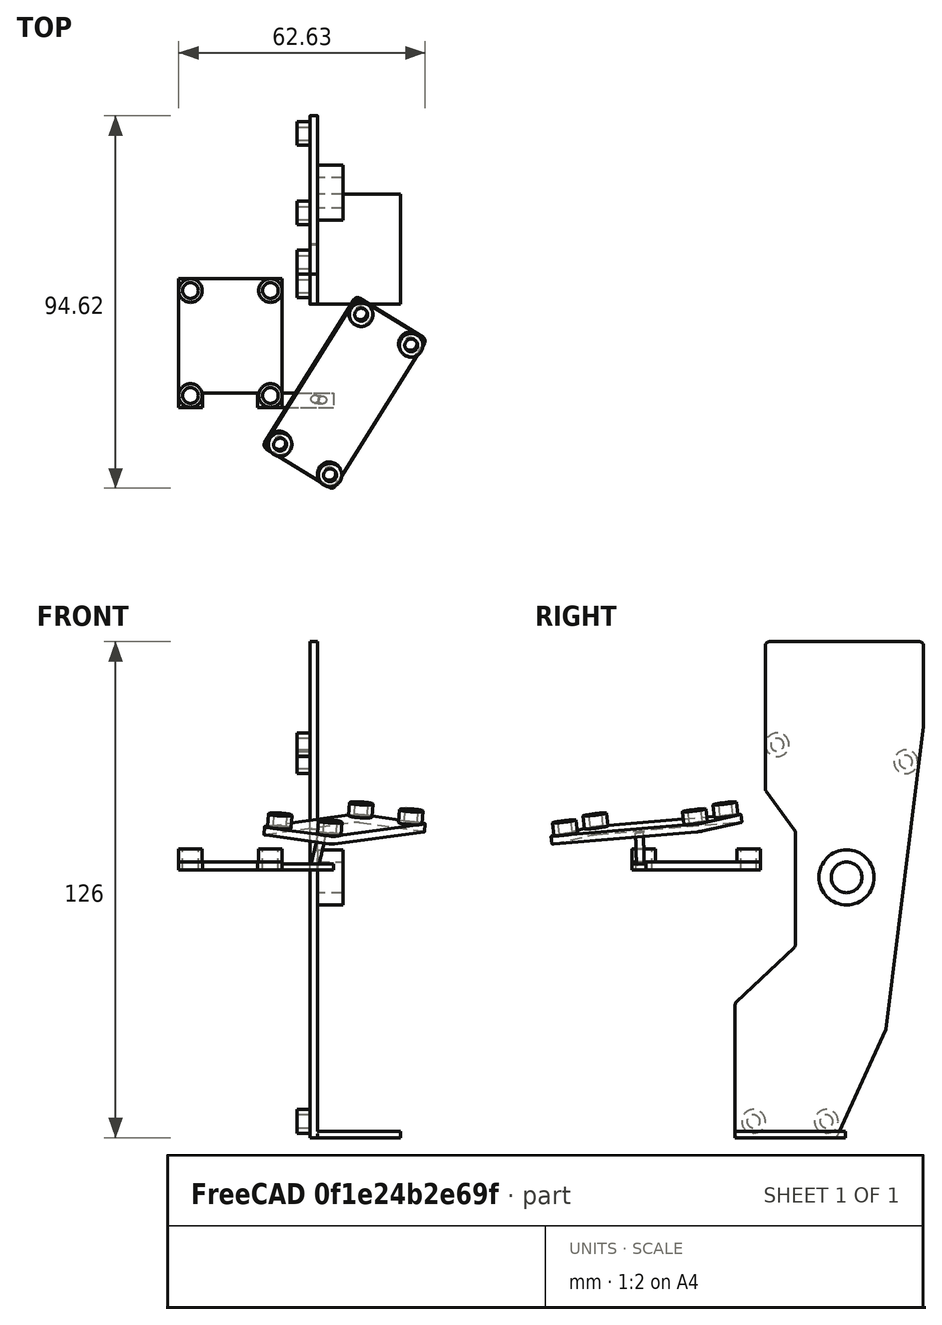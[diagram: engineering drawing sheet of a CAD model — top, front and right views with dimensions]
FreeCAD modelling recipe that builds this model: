
FCSTD DOCUMENT  (FreeCAD 1.0RUnknown)
Label: case-vertical
License: All rights reserved
LicenseURL: https://en.wikipedia.org/wiki/All_rights_reserved
objects: Sketcher::SketchObject×13, PartDesign::Pad×10, App::Link×10, App::FeaturePython×10, PartDesign::Body×3, PartDesign::Pocket×2, Assembly::JointGroup×1, Assembly::AssemblyObject×1, App::Part×1
note: 65 computed .brp shape members not serialized (recipe doc carries the construction recipe); baked Part::Feature solids carry a one-line shape summary decoded from their .brp
EXTERNAL_REF file=left.FCStd obj=Board_f9e4
EXTERNAL_REF file=thumbstick-breakout.FCStd obj=Board_bbd4
EXTERNAL_REF file=thumbstick.FCStd obj=Joystick_v6
EXTERNAL_REF file=thumb-cluster.FCStd obj=Board_58ce
EXTERNAL_REF file=caps.FCStd obj=Body001
EXTERNAL_REF file=caps.FCStd obj=Body
EXTERNAL_REF file=trackball-holder.FCStd obj=Part

FEATURE [Sketcher::SketchObject] PCB_Sketch_f9e4  label="left"
  ArcFitTolerance = 1e-06
  FullyConstrained = false
  MakeInternals = false
  MapMode = 5
  Placement = pos=(0,0,0) rot=(0,-1,0;1.5708rad)
  sketch-geometry (21):
    g0: LineSegment StartX=48.9342 StartY=15.25 StartZ=0 EndX=77.5946 EndY=15.25 EndZ=0
    g1: LineSegment StartX=27.2503 StartY=38.2054 StartZ=0 EndX=0.583058 EndY=26.0175 EndZ=0
    g2: LineSegment StartX=126 StartY=8.65 StartZ=0 EndX=126 EndY=45.95 EndZ=0
    g3: LineSegment StartX=9e-16 StartY=25.1085 StartZ=0 EndX=0 EndY=1 EndZ=0
    g4: LineSegment StartX=104.439 StartY=47.8424 StartZ=0 EndX=27.5489 EndY=38.289 EndZ=0
    g5: LineSegment StartX=34.5465 StartY=0.317255 StartZ=0 EndX=48.2035 EndY=14.9327 EndZ=0
    g6: LineSegment StartX=104.562 StartY=47.85 StartZ=0 EndX=125 EndY=47.85 EndZ=0
    g7: LineSegment StartX=125 StartY=7.65 StartZ=0 EndX=88.6266 EndY=7.65 EndZ=0
    g8: LineSegment StartX=1 StartY=1e-16 StartZ=0 EndX=33.8158 EndY=-1.6e-15 EndZ=0
    g9: LineSegment StartX=126 StartY=45.95 StartZ=0 EndX=126 EndY=46.85 EndZ=0
    g10: LineSegment StartX=78.291 StartY=14.9676 StartZ=0 EndX=88.0364 EndY=7.84274 EndZ=0
    g11: ArcOfCircle CenterX=27.666 CenterY=37.2959 CenterZ=0 NormalX=0 NormalY=0 NormalZ=-1 AngleXU=1.14211 Radius=1.00001 StartAngle=0 EndAngle=0.311303
    g12: ArcOfCircle CenterX=33.8158 CenterY=1.00002 CenterZ=0 NormalX=0 NormalY=0 NormalZ=-1 AngleXU=-2.39007 Radius=1.00002 StartAngle=0 EndAngle=0.81927
    g13: ArcOfCircle CenterX=48.9342 CenterY=14.25 CenterZ=0 NormalX=0 NormalY=0 NormalZ=-1 AngleXU=0.75152 Radius=1.00002 StartAngle=0 EndAngle=0.81927
    g14: ArcOfCircle CenterX=125 CenterY=46.85 CenterZ=0 NormalX=0 NormalY=0 NormalZ=-1 AngleXU=1.5708 Radius=0.999999 StartAngle=0 EndAngle=1.5708
    g15: ArcOfCircle CenterX=125 CenterY=8.65 CenterZ=0 NormalX=0 NormalY=0 NormalZ=-1 AngleXU=3.14159 Radius=0.999999 StartAngle=0 EndAngle=1.5708
    g16: ArcOfCircle CenterX=88.6266 CenterY=8.65 CenterZ=0 NormalX=0 NormalY=0 NormalZ=-1 AngleXU=-1.57079 Radius=1 StartAngle=0 EndAngle=0.631296
    g17: ArcOfCircle CenterX=104.562 CenterY=46.8498 CenterZ=0 NormalX=0 NormalY=0 NormalZ=-1 AngleXU=1.44719 Radius=1.00016 StartAngle=0 EndAngle=0.123594
    g18: ArcOfCircle CenterX=0.999999 CenterY=0.999999 CenterZ=0 NormalX=0 NormalY=0 NormalZ=-1 AngleXU=-1.5708 Radius=0.999999 StartAngle=0 EndAngle=1.5708
    g19: ArcOfCircle CenterX=1.00007 CenterY=25.1085 CenterZ=0 NormalX=0 NormalY=0 NormalZ=-1 AngleXU=4.52044e-05 Radius=1.00007 StartAngle=0 EndAngle=1.14063
    g20: ArcOfCircle CenterX=77.5946 CenterY=14.25 CenterZ=0 NormalX=0 NormalY=0 NormalZ=-1 AngleXU=1.57078 Radius=0.999961 StartAngle=0 EndAngle=0.770416
  constraints (21):
    c: Coincident(g3,g18)
    c: Coincident(g3,g19)
    c: Coincident(g1,g19)
    c: Coincident(g8,g18)
    c: Coincident(g1,g11)
    c: Coincident(g4,g11)
    c: Coincident(g8,g12)
    c: Coincident(g5,g12)
    c: Coincident(g5,g13)
    c: Coincident(g0,g13)
    c: Coincident(g0,g20)
    c: Coincident(g10,g20)
    c: Coincident(g10,g16)
    c: Coincident(g7,g16)
    c: Coincident(g4,g17)
    c: Coincident(g6,g17)
    c: Coincident(g7,g15)
    c: Coincident(g6,g14)
    c: Coincident(g2,g15)
    c: Coincident(g2,g9)
    c: Coincident(g9,g14)
FEATURE [PartDesign::Pad] Pad
  Direction = (-1,0,2e-16)
  Length = 2
  Length2 = 10
  Placement = pos=(0,0,0) rot=(0,-1,0;1.5708rad)
  Profile = -> PCB_Sketch_f9e4
  ReferenceAxis = -> PCB_Sketch_f9e4 [N_Axis]
  Refine = true
  Suppressed = false
  Type = 0
FEATURE [Sketcher::SketchObject] PCB_Sketch_f9e005  label="left holes"
  ArcFitTolerance = 1e-06
  AttachmentSupport = -> [Pad]
  FullyConstrained = false
  MakeInternals = false
  MapMode = 5
  Placement = pos=(-2,0,4e-16) rot=(0,-1,0;1.5708rad)
  sketch-geometry (8):
    g0: Circle CenterX=4.15 CenterY=23.1667 CenterZ=0 NormalX=0 NormalY=0 NormalZ=1 AngleXU=0 Radius=3
    g1: Circle CenterX=4.15 CenterY=4.65 CenterZ=0 NormalX=0 NormalY=0 NormalZ=1 AngleXU=0 Radius=3
    g2: Circle CenterX=95.5 CenterY=43.35 CenterZ=0 NormalX=0 NormalY=0 NormalZ=1 AngleXU=0 Radius=3
    g3: Circle CenterX=99.8333 CenterY=10.6833 CenterZ=0 NormalX=0 NormalY=0 NormalZ=1 AngleXU=0 Radius=3
    g4: Circle CenterX=95.5 CenterY=43.35 CenterZ=0 NormalX=0 NormalY=0 NormalZ=1 AngleXU=0 Radius=1.65
    g5: Circle CenterX=99.8333 CenterY=10.6833 CenterZ=0 NormalX=0 NormalY=0 NormalZ=1 AngleXU=0 Radius=1.65
    g6: Circle CenterX=4.15 CenterY=23.1667 CenterZ=0 NormalX=0 NormalY=0 NormalZ=1 AngleXU=0 Radius=1.65
    g7: Circle CenterX=4.15 CenterY=4.65 CenterZ=0 NormalX=0 NormalY=0 NormalZ=1 AngleXU=0 Radius=1.65
  constraints (12):
    c: Diameter(g0) = 6
    c: Diameter(g1) = 6
    c: Diameter(g2) = 6
    c: Diameter(g3) = 6
    c: Diameter(g4) = 3.3
    c: Coincident(g4,g2)
    c: Diameter(g5) = 3.3
    c: Coincident(g5,g3)
    c: Diameter(g6) = 3.3
    c: Coincident(g6,g0)
    c: Diameter(g7) = 3.3
    c: Coincident(g7,g1)
FEATURE [PartDesign::Pad] Pad003
  BaseFeature = -> Pad
  Direction = (-1,0,2e-16)
  Length = 3.3
  Length2 = 10
  Placement = pos=(0,0,0) rot=(0,-1,0;1.5708rad)
  Profile = -> PCB_Sketch_f9e005
  ReferenceAxis = -> PCB_Sketch_f9e005 [N_Axis]
  Refine = true
  Suppressed = false
  Type = 0
FEATURE [Sketcher::SketchObject] Sketch  label="tindie"
  ArcFitTolerance = 1e-06
  AttachmentSupport = -> [XY_Plane001]
  FullyConstrained = true
  MakeInternals = false
  MapMode = 5
  sketch-geometry (4):
    g0: LineSegment StartX=0 StartY=0 StartZ=0 EndX=21 EndY=0 EndZ=0
    g1: LineSegment StartX=21 StartY=0 StartZ=0 EndX=21 EndY=28 EndZ=0
    g2: LineSegment StartX=21 StartY=28 StartZ=0 EndX=0 EndY=28 EndZ=0
    g3: LineSegment StartX=0 StartY=28 StartZ=0 EndX=0 EndY=0 EndZ=0
  constraints (11):
    c: Coincident(g0,g1)
    c: Coincident(g1,g2)
    c: Coincident(g2,g3)
    c: Coincident(g3,g0)
    c: Horizontal(g0)
    c: Horizontal(g2)
    c: Vertical(g1)
    c: Vertical(g3)
    c: Coincident(g0,g-1)
    c: DistanceY(g1,g1) = 28
    c: DistanceX(g2,g2) = 21
FEATURE [Sketcher::SketchObject] PCB_Sketch_58ce002  label="thumb"
  ArcFitTolerance = 1e-06
  FullyConstrained = false
  MakeInternals = false
  sketch-geometry (8):
    g0: LineSegment StartX=21 StartY=44 StartZ=0 EndX=21 EndY=1 EndZ=0
    g1: LineSegment StartX=20 StartY=1e-16 StartZ=0 EndX=1 EndY=0 EndZ=0
    g2: LineSegment StartX=1 StartY=45 StartZ=0 EndX=20 EndY=45 EndZ=0
    g3: LineSegment StartX=1e-16 StartY=1 StartZ=0 EndX=3.3e-15 EndY=44 EndZ=0
    g4: ArcOfCircle CenterX=20 CenterY=44 CenterZ=0 NormalX=0 NormalY=0 NormalZ=-1 AngleXU=1.5708 Radius=0.999999 StartAngle=0 EndAngle=1.5708
    g5: ArcOfCircle CenterX=0.999999 CenterY=0.999999 CenterZ=0 NormalX=0 NormalY=0 NormalZ=-1 AngleXU=-1.5708 Radius=0.999999 StartAngle=0 EndAngle=1.5708
    g6: ArcOfCircle CenterX=20 CenterY=0.999999 CenterZ=0 NormalX=0 NormalY=0 NormalZ=-1 AngleXU=3.14159 Radius=0.999999 StartAngle=0 EndAngle=1.5708
    g7: ArcOfCircle CenterX=0.999999 CenterY=44 CenterZ=0 NormalX=0 NormalY=0 NormalZ=-1 AngleXU=-7.47076e-07 Radius=0.999999 StartAngle=0 EndAngle=1.5708
  constraints (8):
    c: Coincident(g3,g5)
    c: Coincident(g3,g7)
    c: Coincident(g1,g5)
    c: Coincident(g2,g7)
    c: Coincident(g1,g6)
    c: Coincident(g2,g4)
    c: Coincident(g0,g6)
    c: Coincident(g0,g4)
FEATURE [Sketcher::SketchObject] Sketch001  label="thumbstick pcb"
  ArcFitTolerance = 1e-06
  FullyConstrained = false
  MakeInternals = false
  sketch-geometry (8):
    g0: LineSegment [constr] StartX=2.54 StartY=29.21 StartZ=0 EndX=2.54 EndY=2.54 EndZ=0
    g1: LineSegment [constr] StartX=2.54 StartY=2.54 StartZ=0 EndX=22.86 EndY=2.54 EndZ=0
    g2: LineSegment [constr] StartX=22.86 StartY=2.54 StartZ=0 EndX=22.86 EndY=29.21 EndZ=0
    g3: LineSegment [constr] StartX=22.86 StartY=29.21 StartZ=0 EndX=2.54 EndY=29.21 EndZ=0
    g4: LineSegment StartX=-0.46 StartY=32.21 StartZ=0 EndX=-0.46 EndY=-0.46 EndZ=0
    g5: LineSegment StartX=-0.46 StartY=-0.46 StartZ=0 EndX=25.86 EndY=-0.46 EndZ=0
    g6: LineSegment StartX=25.86 StartY=-0.46 StartZ=0 EndX=25.86 EndY=32.21 EndZ=0
    g7: LineSegment StartX=25.86 StartY=32.21 StartZ=0 EndX=-0.46 EndY=32.21 EndZ=0
  constraints (20):
    c: Coincident(g0,g1)
    c: Coincident(g1,g2)
    c: Coincident(g2,g3)
    c: Coincident(g3,g0)
    c: Vertical(g0)
    c: Vertical(g2)
    c: Horizontal(g1)
    c: Horizontal(g3)
    c: Coincident(g4,g5)
    c: Coincident(g5,g6)
    c: Coincident(g6,g7)
    c: Coincident(g7,g4)
    c: Vertical(g4)
    c: Vertical(g6)
    c: Horizontal(g5)
    c: Horizontal(g7)
    c: Distance(g7,g3) = 3
    c: Distance(g5,g1) = 3
    c: Distance(g6,g2) = 3
    c: Distance(g4,g0) = 3
FEATURE [PartDesign::Pad] Pad009
  Direction = (0,0,1)
  Length = 2
  Length2 = 10
  Profile = -> Sketch001
  ReferenceAxis = -> Sketch001 [N_Axis]
  Refine = true
  Suppressed = false
  Type = 0
FEATURE [Sketcher::SketchObject] Sketch004  label="thumbstick holes"
  ArcFitTolerance = 1e-06
  AttacherType = Attacher::AttachEngine3D
  AttachmentSupport = -> [Pad009]
  FullyConstrained = false
  MakeInternals = false
  MapMode = 5
  Placement = pos=(0,0,2) rot=(0,0,1;0rad)
  sketch-geometry (8):
    g0: Circle CenterX=2.54 CenterY=29.21 CenterZ=0 NormalX=0 NormalY=0 NormalZ=1 AngleXU=0 Radius=3
    g1: Circle CenterX=22.86 CenterY=29.21 CenterZ=0 NormalX=0 NormalY=0 NormalZ=1 AngleXU=0 Radius=3
    g2: Circle CenterX=22.86 CenterY=2.54 CenterZ=0 NormalX=0 NormalY=0 NormalZ=1 AngleXU=0 Radius=3
    g3: Circle CenterX=2.54 CenterY=2.54 CenterZ=0 NormalX=0 NormalY=0 NormalZ=1 AngleXU=0 Radius=3
    g4: Circle CenterX=2.54 CenterY=29.21 CenterZ=0 NormalX=0 NormalY=0 NormalZ=1 AngleXU=0 Radius=2
    g5: Circle CenterX=22.86 CenterY=29.21 CenterZ=0 NormalX=0 NormalY=0 NormalZ=1 AngleXU=0 Radius=2
    g6: Circle CenterX=22.86 CenterY=2.54 CenterZ=0 NormalX=0 NormalY=0 NormalZ=1 AngleXU=0 Radius=2
    g7: Circle CenterX=2.54 CenterY=2.54 CenterZ=0 NormalX=0 NormalY=0 NormalZ=1 AngleXU=0 Radius=2
  constraints (12):
    c: Diameter(g0) = 6
    c: Diameter(g1) = 6
    c: Diameter(g2) = 6
    c: Diameter(g3) = 6
    c: Diameter(g4) = 4
    c: Coincident(g4,g0)
    c: Diameter(g5) = 4
    c: Coincident(g5,g1)
    c: Diameter(g6) = 4
    c: Coincident(g6,g2)
    c: Diameter(g7) = 4
    c: Coincident(g7,g3)
FEATURE [PartDesign::Pad] Pad010
  BaseFeature = -> Pad009
  Direction = (0,0,1)
  Length = 3.3
  Length2 = 10
  Profile = -> Sketch004
  ReferenceAxis = -> Sketch004 [N_Axis]
  Refine = true
  Suppressed = false
  Type = 0
FEATURE [App::Link] Part001
  LinkedObject = -> Part
FEATURE [App::FeaturePython] GroundedJoint  # Assembly grounded joint (typed FeaturePython)
  ObjectToGround = -> Part001
FEATURE [App::Link] left  label="left001"
  LinkPlacement = pos=(-6.9,7.3e-15,1.6e-15) rot=(0,-1,0;1.5708rad)
  LinkedObject = -> <external left.FCStd>#Board_f9e4
  Placement = pos=(-6.9,7.3e-15,1.6e-15) rot=(0,-1,0;1.5708rad)
FEATURE [App::Link] thumbstick_breakout  label="thumbstick-breakout"
  LinkPlacement = pos=(-34.86,-25.75,74.9) rot=(0,0,1;0rad)
  LinkedObject = -> <external thumbstick-breakout.FCStd>#Board_bbd4
  Placement = pos=(-34.86,-25.75,74.9) rot=(0,0,1;0rad)
FEATURE [App::FeaturePython] Joint  label="Fixed"  # Assembly joint (typed FeaturePython)
  Activated = true
  AngleMax = 0
  AngleMin = 0
  Detach1 = false
  Detach2 = false
  Distance = 0
  Distance2 = 0
  EnableAngleMax = false
  EnableAngleMin = false
  EnableLengthMax = false
  EnableLengthMin = false
  JointType = 0 (Fixed)
  LengthMax = 0
  LengthMin = 0
  Placement1 = pos=(160.16,-88.57,-1.6) rot=(0,0,1;0rad)
  Reference1 = -> Assembly [thumbstick_breakout.Board_Geoms_bbd4.Pcb_bbd4.Edge81,thumbstick_breakout.Board_Geoms_bbd4.Pcb_bbd4.Edge81]
FEATURE [App::FeaturePython] Joint001  label="Fixed001"  # Assembly joint (typed FeaturePython)
  Activated = true
  AngleMax = 0
  AngleMin = 0
  Detach1 = false
  Detach2 = false
  Distance = 0
  Distance2 = 0
  EnableAngleMax = false
  EnableAngleMin = false
  EnableLengthMax = false
  EnableLengthMin = false
  JointType = 0 (Fixed)
  LengthMax = 0
  LengthMin = 0
  Placement1 = pos=(23.65,-84.6833,-1.6) rot=(0,0,1;0rad)
  Placement2 = pos=(-5.3,23.1667,4.15) rot=(0,-1,0;1.5708rad)
  Reference1 = -> Assembly [left.Board_Geoms_f9e4.Pcb_f9e4.Edge111,left.Board_Geoms_f9e4.Pcb_f9e4.Edge111]
  Reference2 = -> Assembly [Part001.Body.Edge92,Part001.Body.Edge92]
FEATURE [PartDesign::Pad] Pad011
  Direction = (0,0,1)
  Length = 2
  Length2 = 10
  Profile = -> PCB_Sketch_58ce002
  ReferenceAxis = -> PCB_Sketch_58ce002 [N_Axis]
  Refine = true
  Suppressed = false
  Type = 0
FEATURE [Sketcher::SketchObject] PCB_Sketch_58ce001  label="thumb-holes"
  ArcFitTolerance = 1e-06
  AttacherType = Attacher::AttachEngine3D
  AttachmentSupport = -> [Pad011]
  FullyConstrained = false
  MakeInternals = false
  MapMode = 5
  Placement = pos=(0,0,2) rot=(0,0,1;0rad)
  sketch-geometry (8):
    g0: Circle CenterX=3 CenterY=42 CenterZ=0 NormalX=0 NormalY=0 NormalZ=1 AngleXU=0 Radius=3
    g1: Circle CenterX=18 CenterY=42 CenterZ=0 NormalX=0 NormalY=0 NormalZ=1 AngleXU=0 Radius=3
    g2: Circle CenterX=18 CenterY=3 CenterZ=0 NormalX=0 NormalY=0 NormalZ=1 AngleXU=0 Radius=3
    g3: Circle CenterX=3 CenterY=3 CenterZ=0 NormalX=0 NormalY=0 NormalZ=1 AngleXU=0 Radius=3
    g4: Circle CenterX=3 CenterY=42 CenterZ=0 NormalX=0 NormalY=0 NormalZ=1 AngleXU=0 Radius=1.65
    g5: Circle CenterX=18 CenterY=42 CenterZ=0 NormalX=0 NormalY=0 NormalZ=1 AngleXU=0 Radius=1.65
    g6: Circle CenterX=18 CenterY=3 CenterZ=0 NormalX=0 NormalY=0 NormalZ=1 AngleXU=0 Radius=1.65
    g7: Circle CenterX=3 CenterY=3 CenterZ=0 NormalX=0 NormalY=0 NormalZ=1 AngleXU=0 Radius=1.65
  constraints (12):
    c: Diameter(g0) = 6
    c: Diameter(g1) = 6
    c: Diameter(g2) = 6
    c: Diameter(g3) = 6
    c: Diameter(g4) = 3.3
    c: Coincident(g4,g0)
    c: Diameter(g5) = 3.3
    c: Coincident(g5,g1)
    c: Diameter(g6) = 3.3
    c: Coincident(g6,g2)
    c: Diameter(g7) = 3.3
    c: Coincident(g7,g3)
FEATURE [PartDesign::Pad] Pad012
  BaseFeature = -> Pad011
  Direction = (0,0,1)
  Length = 3.3
  Length2 = 10
  Profile = -> PCB_Sketch_58ce001
  ReferenceAxis = -> PCB_Sketch_58ce001 [N_Axis]
  Refine = true
  Suppressed = false
  Type = 0
FEATURE [App::Link] Joystick_v6  label="Joystick v6"
  LinkPlacement = pos=(-22.16,-10.937,74.6) rot=(0,0,1;3.14159rad)
  LinkedObject = -> <external thumbstick.FCStd>#Joystick_v6
  Placement = pos=(-22.16,-10.937,74.6) rot=(0,0,1;3.14159rad)
FEATURE [App::Link] thumb_cluster  label="thumb-cluster"
  LinkPlacement = pos=(-13.5716,-36.8519,83.8338) rot=(0.181209,0.166459,-0.969255;0.570723rad)
  LinkedObject = -> <external thumb-cluster.FCStd>#Board_58ce
  Placement = pos=(-13.5716,-36.8519,83.8338) rot=(0.181209,0.166459,-0.969255;0.570723rad)
FEATURE [App::FeaturePython] Joint004  label="Fixed004"  # Assembly joint (typed FeaturePython)
  Activated = true
  AngleMax = 0
  AngleMin = 0
  Detach1 = false
  Detach2 = false
  Distance = 0
  Distance2 = 0
  EnableAngleMax = false
  EnableAngleMin = false
  EnableLengthMax = false
  EnableLengthMin = false
  JointType = 0 (Fixed)
  LengthMax = 0
  LengthMin = 0
  Placement1 = pos=(37.5,-27,-1.6) rot=(0,0,1;0rad)
  Placement2 = pos=(18,42,5.3) rot=(0,0,1;0rad)
  Reference1 = -> Assembly [thumb_cluster.Board_Geoms_58ce.Pcb_58ce.Edge102,thumb_cluster.Board_Geoms_58ce.Pcb_58ce.Edge102]
  Reference2 = -> Assembly [Part001.Body001.Edge54,Part001.Body001.Edge54]
FEATURE [App::Link] stem
  LinkPlacement = pos=(1.19724,-34.4065,86.1408) rot=(0.181209,0.166459,-0.969255;0.570723rad)
  LinkedObject = -> <external caps.FCStd>#Body001
  Placement = pos=(1.19724,-34.4065,86.1408) rot=(0.181209,0.166459,-0.969255;0.570723rad)
FEATURE [App::Link] stem001
  LinkPlacement = pos=(11.0023,-18.7101,87.4829) rot=(0.181209,0.166459,-0.969255;0.570723rad)
  LinkedObject = -> <external caps.FCStd>#Body001
  Placement = pos=(11.0023,-18.7101,87.4829) rot=(0.181209,0.166459,-0.969255;0.570723rad)
FEATURE [App::Link] xring
  LinkPlacement = pos=(1.55737,-35.1226,91.8852) rot=(0.181209,0.166459,-0.969255;0.570723rad)
  LinkedObject = -> <external caps.FCStd>#Body
  Placement = pos=(1.55737,-35.1226,91.8852) rot=(0.181209,0.166459,-0.969255;0.570723rad)
FEATURE [App::Link] xring001
  LinkPlacement = pos=(11.3625,-19.4262,93.2272) rot=(0.181209,0.166459,-0.969255;0.570723rad)
  LinkedObject = -> <external caps.FCStd>#Body
  Placement = pos=(11.3625,-19.4262,93.2272) rot=(0.181209,0.166459,-0.969255;0.570723rad)
FEATURE [App::FeaturePython] Joint008  label="Fixed005"  # Assembly joint (typed FeaturePython)
  Activated = true
  AngleMax = 0
  AngleMin = 0
  Detach1 = false
  Detach2 = false
  Distance = 0
  Distance2 = 0
  EnableAngleMax = false
  EnableAngleMin = false
  EnableLengthMax = false
  EnableLengthMin = false
  JointType = 0 (Fixed)
  LengthMax = 0
  LengthMin = 0
  Offset1 = pos=(2,0,0) rot=(0,0,1;0rad)
  Offset2 = pos=(0,0,0) rot=(0,0,-1;1.5708rad)
  Placement1 = pos=(-1.8e-15,-1.05,2) rot=(0.707107,0,0.707107;3.14159rad)
  Placement2 = pos=(0.689429,-0.689429,4.9) rot=(-0.678598,-0.281085,-0.678598;2.59356rad)
  Reference1 = -> Assembly [stem.Edge4,stem.Edge4]
  Reference2 = -> Assembly [thumb_cluster.Step_Models_58ce.Top_58ce.SKRHADE.Part__Feature.Edge671,thumb_cluster.Step_Models_58ce.Top_58ce.SKRHADE.Part__Feature.Edge671]
FEATURE [App::FeaturePython] Joint009  label="Fixed006"  # Assembly joint (typed FeaturePython)
  Activated = true
  AngleMax = 0
  AngleMin = 0
  Detach1 = false
  Detach2 = false
  Distance = 0
  Distance2 = 0
  EnableAngleMax = false
  EnableAngleMin = false
  EnableLengthMax = false
  EnableLengthMin = false
  JointType = 0 (Fixed)
  LengthMax = 0
  LengthMin = 0
  Placement2 = pos=(0,0,5.8) rot=(0,0,1;0rad)
  Reference1 = -> Assembly [xring.Edge17,xring.Edge17]
  Reference2 = -> Assembly [stem.Edge8,stem.Edge8]
FEATURE [App::FeaturePython] Joint010  label="Fixed007"  # Assembly joint (typed FeaturePython)
  Activated = true
  AngleMax = 0
  AngleMin = 0
  Detach1 = false
  Detach2 = false
  Distance = 0
  Distance2 = 0
  EnableAngleMax = false
  EnableAngleMin = false
  EnableLengthMax = false
  EnableLengthMin = false
  JointType = 0 (Fixed)
  LengthMax = 0
  LengthMin = 0
  Offset1 = pos=(2,0,0) rot=(0,0,1;0rad)
  Offset2 = pos=(0,0,0) rot=(0,0,-1;1.5708rad)
  Placement1 = pos=(3.6e-15,-1.05,2) rot=(0.707107,0,0.707107;3.14159rad)
  Placement2 = pos=(0.689429,-0.689429,4.9) rot=(-0.678598,-0.281085,-0.678598;2.59356rad)
  Reference1 = -> Assembly [stem001.Edge4,stem001.Edge4]
  Reference2 = -> Assembly [thumb_cluster.Step_Models_58ce.Top_58ce.S6_SKRHADE_66ce9957abdd_ln_.Part__Feature.Edge671,thumb_cluster.Step_Models_58ce.Top_58ce.S6_SKRHADE_66ce9957abdd_ln_.Part__Feature.Edge671]
FEATURE [App::FeaturePython] Joint011  label="Fixed008"  # Assembly joint (typed FeaturePython)
  Activated = true
  AngleMax = 0
  AngleMin = 0
  Detach1 = false
  Detach2 = false
  Distance = 0
  Distance2 = 0
  EnableAngleMax = false
  EnableAngleMin = false
  EnableLengthMax = false
  EnableLengthMin = false
  JointType = 0 (Fixed)
  LengthMax = 0
  LengthMin = 0
  Placement2 = pos=(-3.6e-15,1.8e-15,5.8) rot=(0,0,1;0rad)
  Reference1 = -> Assembly [xring001.Edge17,xring001.Edge17]
  Reference2 = -> Assembly [stem001.Edge8,stem001.Edge8]
FEATURE [Sketcher::SketchObject] Sketch006
  ArcFitTolerance = 1e-06
  AttachmentSupport = -> [Pad010]
  FullyConstrained = false
  MakeInternals = false
  MapMode = 5
  Placement = pos=(-0.46,0,0) rot=(0.57735,-0.57735,-0.57735;2.0944rad)
  sketch-geometry (4):
    g0: LineSegment StartX=-32.2214 StartY=1.56343 StartZ=0 EndX=-32.2214 EndY=0 EndZ=0
    g1: LineSegment StartX=-32.2214 StartY=0 StartZ=0 EndX=-28.6163 EndY=0 EndZ=0
    g2: LineSegment StartX=-28.6163 StartY=0 StartZ=0 EndX=-28.6163 EndY=1.56343 EndZ=0
    g3: LineSegment StartX=-28.6163 StartY=1.56343 StartZ=0 EndX=-32.2214 EndY=1.56343 EndZ=0
  constraints (9):
    c: Coincident(g0,g1)
    c: Coincident(g1,g2)
    c: Coincident(g2,g3)
    c: Coincident(g3,g0)
    c: Vertical(g0)
    c: Vertical(g2)
    c: Horizontal(g1)
    c: Horizontal(g3)
    c: PointOnObject(g1,g-1)
FEATURE [PartDesign::Pad] Pad013
  BaseFeature = -> Pad010
  Direction = (-1,0,0)
  Length = 13
  Length2 = 10
  Profile = -> Sketch006
  ReferenceAxis = -> Sketch006 [N_Axis]
  Refine = true
  Suppressed = false
  Type = 0
FEATURE [Sketcher::SketchObject] Sketch007
  ArcFitTolerance = 1e-06
  AttachmentSupport = -> [Pad013]
  FullyConstrained = true
  MakeInternals = false
  MapMode = 5
  Placement = pos=(0,0,1.56343) rot=(0,0,1;0rad)
FEATURE [Sketcher::SketchObject] Sketch008
  ArcFitTolerance = 1e-06
  AttachmentSupport = -> [Pad012]
  FullyConstrained = false
  MakeInternals = false
  MapMode = 5
  Placement = pos=(0,0,0) rot=(1,0,0;3.14159rad)
  sketch-geometry (1):
    g0: Circle CenterX=6.77488 CenterY=-17.9445 CenterZ=0 NormalX=0 NormalY=0 NormalZ=1 AngleXU=0 Radius=1
  constraints (1):
    c: Diameter(g0) = 2
FEATURE [PartDesign::Pad] Pad014
  BaseFeature = -> Pad012
  Direction = (-0.6,-1.1,-6.5)
  Length = 8.2
  Length2 = 10
  Profile = -> Sketch008
  ReferenceAxis = -> Sketch008 [N_Axis]
  Refine = true
  Suppressed = false
  Type = 0
  UseCustomVector = true
FEATURE [PartDesign::Body] Body001  label="Thumb"
  AllowCompound = false
  Group = -> [PCB_Sketch_58ce002,PCB_Sketch_58ce001,Pad011,Pad012,Sketch008,Pad014]
  Origin = -> Origin002
  Placement = pos=(-14,-36,77) rot=(-0.86,-0.79,4.6;5.71246rad)
  Tip = -> Pad014
FEATURE [App::Link] Part002
  LinkPlacement = pos=(-22.2918,-9.63135,74.7609) rot=(0,0,1;0rad)
  LinkedObject = -> <external trackball-holder.FCStd>#Part
  Placement = pos=(-22.2918,-9.63135,74.7609) rot=(0,0,1;0rad)
FEATURE [Sketcher::SketchObject] Sketch015
  ArcFitTolerance = 1e-06
  AttachmentSupport = -> [Pad013]
  ExternalGeometry = -> [Pad013]
  FullyConstrained = true
  MakeInternals = false
  MapMode = 5
  Placement = pos=(0,0,5.3) rot=(0,0,1;0rad)
  sketch-geometry (4):
    g0: Circle CenterX=2.54 CenterY=29.21 CenterZ=0 NormalX=0 NormalY=0 NormalZ=1 AngleXU=0 Radius=2
    g1: Circle CenterX=22.86 CenterY=29.21 CenterZ=0 NormalX=0 NormalY=0 NormalZ=1 AngleXU=0 Radius=2
    g2: Circle CenterX=22.86 CenterY=2.54 CenterZ=0 NormalX=0 NormalY=0 NormalZ=1 AngleXU=0 Radius=2
    g3: Circle CenterX=2.54 CenterY=2.54 CenterZ=0 NormalX=0 NormalY=0 NormalZ=1 AngleXU=0 Radius=2
  constraints (8):
    c: Coincident(g0,g-3)
    c: Equal(g0,g-3)
    c: Coincident(g1,g-4)
    c: Equal(g1,g-4)
    c: Coincident(g2,g-5)
    c: Equal(g2,g-5)
    c: Coincident(g3,g-6)
    c: Equal(g3,g-6)
FEATURE [PartDesign::Pocket] Pocket
  BaseFeature = -> Pad013
  Direction = (0,0,-1)
  Length = 6
  Length2 = 5
  Profile = -> Sketch015
  ReferenceAxis = -> Sketch015 [N_Axis]
  Refine = true
  Suppressed = false
  Type = 1
FEATURE [Sketcher::SketchObject] Sketch016
  ArcFitTolerance = 1e-06
  AttachmentSupport = -> [Pocket]
  ExternalGeometry = -> [Pocket]
  FullyConstrained = false
  MakeInternals = false
  MapMode = 5
  Placement = pos=(0,0,2) rot=(0,0,1;0rad)
  sketch-geometry (4):
    g0: LineSegment StartX=5.79831 StartY=32.21 StartZ=0 EndX=5.79831 EndY=28.6463 EndZ=0
    g1: LineSegment StartX=5.79831 StartY=28.6463 StartZ=0 EndX=19.7769 EndY=28.6463 EndZ=0
    g2: LineSegment StartX=19.7769 StartY=28.6463 StartZ=0 EndX=19.7769 EndY=32.21 EndZ=0
    g3: LineSegment StartX=19.7769 StartY=32.21 StartZ=0 EndX=5.79831 EndY=32.21 EndZ=0
  constraints (9):
    c: Coincident(g0,g1)
    c: Coincident(g1,g2)
    c: Coincident(g2,g3)
    c: Coincident(g3,g0)
    c: Vertical(g0)
    c: Vertical(g2)
    c: Horizontal(g1)
    c: Horizontal(g3)
    c: PointOnObject(g0,g-3)
FEATURE [PartDesign::Pocket] Pocket001
  BaseFeature = -> Pocket
  Direction = (0,0,-1)
  Length = 5
  Length2 = 5
  Profile = -> Sketch016
  ReferenceAxis = -> Sketch016 [N_Axis]
  Refine = true
  Suppressed = false
  Type = 1
FEATURE [PartDesign::Body] Body002  label="Thumbstick"
  AllowCompound = false
  Group = -> [Sketch004,Sketch001,Pad009,Pad010,Sketch006,Pad013,Sketch007,Sketch015,Pocket,Sketch016,Pocket001]
  Origin = -> Origin003
  Placement = pos=(-9.46,6,68) rot=(0,0,1;3.14159rad)
  Tip = -> Pocket001
FEATURE [App::FeaturePython] Joint015  label="Fixed009"  # Assembly joint (typed FeaturePython)
  Activated = true
  AngleMax = 0
  AngleMin = 0
  Detach1 = false
  Detach2 = false
  Distance = 0
  Distance2 = 0
  EnableAngleMax = false
  EnableAngleMin = false
  EnableLengthMax = false
  EnableLengthMin = false
  JointType = 0 (Fixed)
  LengthMax = 0
  LengthMin = 0
  Placement1 = pos=(139.84,-88.57,-1.6) rot=(0,0,1;0rad)
  Placement2 = pos=(22.86,2.54,5.3) rot=(0,0,1;0rad)
  Reference1 = -> Assembly [thumbstick_breakout.Board_Geoms_bbd4.Pcb_bbd4.Edge51,thumbstick_breakout.Board_Geoms_bbd4.Pcb_bbd4.Edge51]
  Reference2 = -> Assembly [Part001.Body002.Edge59,Part001.Body002.Edge59]
FEATURE [App::FeaturePython] Joint016  label="Fixed010"  # Assembly joint (typed FeaturePython)
  Activated = true
  AngleMax = 0
  AngleMin = 0
  Detach1 = false
  Detach2 = false
  Distance = 0
  Distance2 = 0
  EnableAngleMax = false
  EnableAngleMin = false
  EnableLengthMax = false
  EnableLengthMin = false
  JointType = 0 (Fixed)
  LengthMax = 0
  LengthMin = 0
  Offset2 = pos=(0,0,-4) rot=(0,0,1;3.14159rad)
  Placement1 = pos=(2.5,9.75,-3.7) rot=(1,0,0;3.14159rad)
  Placement2 = pos=(147.5,-112.717,-4) rot=(0,0,1;3.14159rad)
  Reference1 = -> Assembly [Joystick_v6.COMPOUND.Part__Feature008.Edge2,Joystick_v6.COMPOUND.Part__Feature008.Edge2]
  Reference2 = -> Assembly [thumbstick_breakout.Board_Geoms_bbd4.Pcb_bbd4.Edge17,thumbstick_breakout.Board_Geoms_bbd4.Pcb_bbd4.Edge17]
FEATURE [Assembly::JointGroup] Joints
  Group = -> [GroundedJoint,Joint,Joint001,Joint004,Joint008,Joint009,Joint010,Joint011,Joint015,Joint016]
FEATURE [Assembly::AssemblyObject] Assembly
  Group = -> [Joints,Part001,GroundedJoint,left,thumbstick_breakout,Joint,Joint001,Joystick_v6,thumb_cluster,Joint004,stem,stem001,xring,xring001,Joint008,Joint009,Joint010,Joint011,Part002,Joint015,Joint016]
  Origin = -> Origin004
  Type = Assembly
FEATURE [PartDesign::Pad] Pad015
  BaseFeature = -> Pad003
  Direction = (0,0,1)
  Length = 1.6
  Length2 = 10
  Placement = pos=(0,0,0) rot=(0,-1,0;1.5708rad)
  Profile = -> Sketch
  ReferenceAxis = -> Sketch [N_Axis]
  Refine = true
  Suppressed = false
  Type = 0
FEATURE [Sketcher::SketchObject] Sketch017
  ArcFitTolerance = 1e-06
  AttachmentSupport = -> [Pad015]
  FullyConstrained = false
  MakeInternals = false
  MapMode = 5
  Placement = pos=(1e-16,0,0) rot=(0.707107,0,0.707107;3.14159rad)
  sketch-geometry (2):
    g0: Circle CenterX=66.1396 CenterY=-28.2921 CenterZ=0 NormalX=0 NormalY=0 NormalZ=1 AngleXU=0 Radius=3.9
    g1: Circle CenterX=66.1396 CenterY=-28.2921 CenterZ=0 NormalX=0 NormalY=0 NormalZ=1 AngleXU=0 Radius=7
  constraints (3):
    c: Diameter(g0) = 7.8
    c: Diameter(g1) = 14
    c: Coincident(g1,g0)
FEATURE [PartDesign::Pad] Pad016
  BaseFeature = -> Pad015
  Direction = (1,0,-2e-16)
  Length = 6.5
  Length2 = 10
  Placement = pos=(0,0,0) rot=(0,-1,0;1.5708rad)
  Profile = -> Sketch017
  ReferenceAxis = -> Sketch017 [N_Axis]
  Refine = true
  Suppressed = false
  Type = 0
FEATURE [PartDesign::Body] Body  label="Left"
  AllowCompound = true
  Group = -> [PCB_Sketch_f9e005,PCB_Sketch_f9e4,Pad,Pad003,Sketch,Pad015,Sketch017,Pad016]
  Origin = -> Origin001
  Tip = -> Pad016
FEATURE [App::Part] Part
  Group = -> [Body,Body001,Body002]
  Origin = -> Origin

RESOLVED EXTERNAL PARTS (link-assembly join: the EXTERNAL_REF files above that resolve inside this repo's crawl, each included once):
---- part caps.FCStd = doc fcstd_863bb0473ba7 ----
FCSTD DOCUMENT  (FreeCAD 1.0RUnknown)
Label: caps
License: All rights reserved
LicenseURL: https://en.wikipedia.org/wiki/All_rights_reserved
objects: Sketcher::SketchObject×9, PartDesign::Pocket×3, PartDesign::Pad×2, PartDesign::Body×2, PartDesign::Plane×2, PartDesign::Chamfer×2, PartDesign::AdditiveLoft×1, PartDesign::SubtractiveLoft×1, PartDesign::Fillet×1
note: 52 computed .brp shape members not serialized (recipe doc carries the construction recipe); baked Part::Feature solids carry a one-line shape summary decoded from their .brp

FEATURE [Sketcher::SketchObject] Sketch006
  ArcFitTolerance = 1e-06
  AttachmentSupport = -> [XY_Plane001]
  FullyConstrained = true
  MakeInternals = false
  MapMode = 5
  sketch-geometry (1):
    g0: Circle CenterX=0 CenterY=0 CenterZ=0 NormalX=0 NormalY=0 NormalZ=1 AngleXU=0 Radius=3
  constraints (2):
    c: Diameter(g0) = 6
    c: Coincident(g0,g-1)
FEATURE [PartDesign::Pad] Pad001
  Direction = (0,0,1)
  Length = 5.8
  Length2 = 10
  Profile = -> Sketch006
  ReferenceAxis = -> Sketch006 [N_Axis]
  Refine = true
  Suppressed = false
  Type = 0
FEATURE [Sketcher::SketchObject] Sketch007
  ArcFitTolerance = 1e-06
  AttachmentSupport = -> [XY_Plane001]
  FullyConstrained = true
  MakeInternals = false
  MapMode = 5
  sketch-geometry (5):
    g0: LineSegment StartX=-1.05 StartY=-1.05 StartZ=0 EndX=1.05 EndY=-1.05 EndZ=0
    g1: LineSegment StartX=1.05 StartY=-1.05 StartZ=0 EndX=1.05 EndY=1.05 EndZ=0
    g2: LineSegment StartX=1.05 StartY=1.05 StartZ=0 EndX=-1.05 EndY=1.05 EndZ=0
    g3: LineSegment StartX=-1.05 StartY=1.05 StartZ=0 EndX=-1.05 EndY=-1.05 EndZ=0
    g4: GeomPoint [constr] X=0 Y=0 Z=0
  constraints (12):
    c: Coincident(g0,g1)
    c: Coincident(g1,g2)
    c: Coincident(g2,g3)
    c: Coincident(g3,g0)
    c: Horizontal(g0)
    c: Horizontal(g2)
    c: Vertical(g1)
    c: Vertical(g3)
    c: Symmetric(g2,g0,g4)
    c: Distance(g1,g3) = 2.1
    c: Distance(g0,g2) = 2.1
    c: Coincident(g4,g-1)
FEATURE [PartDesign::Pocket] Pocket001
  BaseFeature = -> Pad001
  Direction = (0,0,-1)
  Length = 2.2
  Length2 = 5
  Profile = -> Sketch007
  ReferenceAxis = -> Sketch007 [N_Axis]
  Refine = true
  Reversed = true
  Suppressed = false
  Type = 0
FEATURE [Sketcher::SketchObject] Sketch008
  ArcFitTolerance = 1e-06
  AttachmentSupport = -> [Pocket001]
  FullyConstrained = true
  MakeInternals = false
  MapMode = 5
  Placement = pos=(0,0,5.8) rot=(0,0,1;0rad)
  sketch-geometry (1):
    g0: Circle CenterX=0 CenterY=0 CenterZ=0 NormalX=0 NormalY=0 NormalZ=1 AngleXU=0 Radius=1.65
  constraints (2):
    c: Diameter(g0) = 3.3
    c: Coincident(g0,g-1)
FEATURE [PartDesign::Pocket] Pocket002
  BaseFeature = -> Pocket001
  Direction = (0,0,-1)
  Length = 3.3
  Length2 = 5
  Profile = -> Sketch008
  ReferenceAxis = -> Sketch008 [N_Axis]
  Refine = true
  Suppressed = false
  Type = 0
FEATURE [PartDesign::Body] Body001  label="stem"
  AllowCompound = false
  Group = -> [Sketch006,Pad001,Sketch007,Pocket001,Sketch008,Pocket002]
  Origin = -> Origin001
  Tip = -> Pocket002
FEATURE [Sketcher::SketchObject] Sketch
  ArcFitTolerance = 1e-06
  AttachmentSupport = -> [XY_Plane]
  FullyConstrained = true
  MakeInternals = false
  MapMode = 5
  sketch-geometry (1):
    g0: Circle CenterX=0 CenterY=0 CenterZ=0 NormalX=0 NormalY=0 NormalZ=1 AngleXU=0 Radius=5.85
  constraints (2):
    c: Coincident(g0,g-1)
    c: Diameter(g0) = 11.7
FEATURE [PartDesign::Pad] Pad
  Direction = (0,0,1)
  Length = 1.3
  Length2 = 10
  Profile = -> Sketch
  ReferenceAxis = -> Sketch [N_Axis]
  Refine = true
  Suppressed = false
  Type = 0
FEATURE [Sketcher::SketchObject] Sketch001
  ArcFitTolerance = 1e-06
  AttachmentSupport = -> [Pad]
  FullyConstrained = true
  MakeInternals = false
  MapMode = 5
  Placement = pos=(0,0,1.3) rot=(0,0,1;0rad)
  sketch-geometry (1):
    g0: Circle CenterX=0 CenterY=0 CenterZ=0 NormalX=0 NormalY=0 NormalZ=1 AngleXU=0 Radius=4.35
  constraints (2):
    c: Diameter(g0) = 8.7
    c: Coincident(g0,g-1)
FEATURE [PartDesign::Plane] DatumPlane
  AttachmentOffset = pos=(0,0,1.3) rot=(0,0,1;0rad)
  AttachmentSupport = -> [Sketch001]
  Length = 60
  MapMode = 45
  Placement = pos=(2.07e-14,3e-16,2.6) rot=(0,0,1;0rad)
  ResizeMode = 0
  Width = 60
FEATURE [Sketcher::SketchObject] Sketch002
  ArcFitTolerance = 1e-06
  AttachmentSupport = -> [DatumPlane]
  FullyConstrained = true
  MakeInternals = false
  MapMode = 5
  Placement = pos=(2.07e-14,3e-16,2.6) rot=(0,0,1;0rad)
  sketch-geometry (1):
    g0: Circle CenterX=0 CenterY=0 CenterZ=0 NormalX=0 NormalY=0 NormalZ=1 AngleXU=0 Radius=5.35
  constraints (2):
    c: Diameter(g0) = 10.7
    c: Coincident(g0,g-1)
FEATURE [PartDesign::AdditiveLoft] AdditiveLoft
  BaseFeature = -> Pad
  Closed = false
  Profile = -> Sketch002
  Refine = true
  Ruled = false
  Sections = -> [Sketch001]
  Suppressed = false
FEATURE [Sketcher::SketchObject] Sketch003
  ArcFitTolerance = 1e-06
  AttachmentSupport = -> [DatumPlane]
  FullyConstrained = true
  MakeInternals = false
  MapMode = 5
  Placement = pos=(2.07e-14,3e-16,2.6) rot=(0,0,1;0rad)
  sketch-geometry (1):
    g0: Circle CenterX=0 CenterY=0 CenterZ=0 NormalX=0 NormalY=0 NormalZ=1 AngleXU=0 Radius=4.85
  constraints (2):
    c: Diameter(g0) = 9.7
    c: Coincident(g0,g-1)
FEATURE [PartDesign::Plane] DatumPlane001
  AttachmentOffset = pos=(0,0,-1.3) rot=(0,0,1;0rad)
  AttachmentSupport = -> [AdditiveLoft]
  Length = 60
  MapMode = 5
  Placement = pos=(0,0,1.3) rot=(0,0,1;0rad)
  ResizeMode = 0
  Width = 60
FEATURE [Sketcher::SketchObject] Sketch004
  ArcFitTolerance = 1e-06
  AttachmentSupport = -> [DatumPlane001]
  FullyConstrained = true
  MakeInternals = false
  MapMode = 5
  Placement = pos=(0,0,1.3) rot=(0,0,1;0rad)
  sketch-geometry (1):
    g0: Circle CenterX=0 CenterY=0 CenterZ=0 NormalX=0 NormalY=0 NormalZ=1 AngleXU=0 Radius=3.85
  constraints (2):
    c: Diameter(g0) = 7.7
    c: Coincident(g0,g-1)
FEATURE [PartDesign::SubtractiveLoft] SubtractiveLoft
  BaseFeature = -> AdditiveLoft
  Closed = false
  Profile = -> Sketch003
  Refine = true
  Ruled = false
  Sections = -> [Sketch004]
  Suppressed = false
FEATURE [Sketcher::SketchObject] Sketch005
  ArcFitTolerance = 1e-06
  AttachmentSupport = -> [SubtractiveLoft]
  FullyConstrained = true
  MakeInternals = false
  MapMode = 5
  Placement = pos=(0,0,1.3) rot=(0,0,1;0rad)
  sketch-geometry (1):
    g0: Circle CenterX=0 CenterY=0 CenterZ=0 NormalX=0 NormalY=0 NormalZ=1 AngleXU=0 Radius=1.25
  constraints (2):
    c: Coincident(g0,g-1)
    c: Diameter(g0) = 2.5
FEATURE [PartDesign::Pocket] Pocket
  BaseFeature = -> SubtractiveLoft
  Direction = (0,0,-1)
  Length = 5
  Length2 = 5
  Profile = -> Sketch005
  ReferenceAxis = -> Sketch005 [N_Axis]
  Refine = true
  Suppressed = false
  Type = 1
FEATURE [PartDesign::Chamfer] Chamfer
  Angle = 30
  Base = -> Pocket [Edge6]
  BaseFeature = -> Pocket
  ChamferType = 2
  FlipDirection = false
  Refine = true
  Size = 1.2
  Size2 = 1
  SupportTransform = false
  Suppressed = false
  UseAllEdges = false
FEATURE [PartDesign::Fillet] Fillet
  Base = -> Chamfer [Edge7]
  BaseFeature = -> Chamfer
  Radius = 1
  Refine = true
  SupportTransform = false
  Suppressed = false
  UseAllEdges = false
FEATURE [PartDesign::Chamfer] Chamfer001
  Angle = 45
  Base = -> Fillet [Edge11]
  BaseFeature = -> Fillet
  ChamferType = 2
  FlipDirection = false
  Refine = true
  Size = 0.3
  Size2 = 1
  SupportTransform = false
  Suppressed = false
  UseAllEdges = false
FEATURE [PartDesign::Body] Body  label="xring"
  AllowCompound = false
  Group = -> [Sketch,Pad,Sketch001,DatumPlane,Sketch002,AdditiveLoft,Sketch003,DatumPlane001,Sketch004,SubtractiveLoft,Sketch005,Pocket,Chamfer,Fillet,Chamfer001]
  Origin = -> Origin
  Tip = -> Chamfer001
---- part left.FCStd = doc fcstd_3019e020500d (78541 chars; too large to inline — full recipe in that document) ----
---- part thumb-cluster.FCStd = doc fcstd_5160b2ce58e3 ----
FCSTD DOCUMENT  (FreeCAD 1.0RUnknown)
Label: thumb-cluster
License: All rights reserved
LicenseURL: https://en.wikipedia.org/wiki/All_rights_reserved
objects: Part::Feature×14, Sketcher::SketchObject×10, App::Link×10, App::Part×6, PartDesign::Pocket×4, PartDesign::Pad×3, PartDesign::Chamfer×3, PartDesign::Thickness×2, PartDesign::Body×2, PartDesign::SubShapeBinder×2, PartDesign::CoordinateSystem×1, PartDesign::ShapeBinder×1
note: 76 computed .brp shape members not serialized (recipe doc carries the construction recipe); baked Part::Feature solids carry a one-line shape summary decoded from their .brp

FEATURE [PartDesign::CoordinateSystem] Local_CS_58ce
  AttacherType = Attacher::AttachEngine3D
  MapMode = 2
FEATURE [Part::Feature] Pcb_58ce
  Placement = pos=(-19.5,69,0) rot=(0,0,1;0rad)
  shape: bbox 21 x 45 x 1.6 mm, 50 faces (baked)
FEATURE [Sketcher::SketchObject] PCB_Sketch_58ce
  ArcFitTolerance = 1e-06
  FullyConstrained = false
  MakeInternals = false
  sketch-geometry (8):
    g0: LineSegment StartX=21 StartY=44 StartZ=0 EndX=21 EndY=1 EndZ=0
    g1: LineSegment StartX=20 StartY=1e-16 StartZ=0 EndX=1 EndY=0 EndZ=0
    g2: LineSegment StartX=1 StartY=45 StartZ=0 EndX=20 EndY=45 EndZ=0
    g3: LineSegment StartX=1e-16 StartY=1 StartZ=0 EndX=3.3e-15 EndY=44 EndZ=0
    g4: ArcOfCircle CenterX=20 CenterY=44 CenterZ=0 NormalX=0 NormalY=0 NormalZ=-1 AngleXU=1.5708 Radius=0.999999 StartAngle=0 EndAngle=1.5708
    g5: ArcOfCircle CenterX=0.999999 CenterY=0.999999 CenterZ=0 NormalX=0 NormalY=0 NormalZ=-1 AngleXU=-1.5708 Radius=0.999999 StartAngle=0 EndAngle=1.5708
    g6: ArcOfCircle CenterX=20 CenterY=0.999999 CenterZ=0 NormalX=0 NormalY=0 NormalZ=-1 AngleXU=3.14159 Radius=0.999999 StartAngle=0 EndAngle=1.5708
    g7: ArcOfCircle CenterX=0.999999 CenterY=44 CenterZ=0 NormalX=0 NormalY=0 NormalZ=-1 AngleXU=-7.47076e-07 Radius=0.999999 StartAngle=0 EndAngle=1.5708
  constraints (8):
    c: Coincident(g3,g5)
    c: Coincident(g3,g7)
    c: Coincident(g1,g5)
    c: Coincident(g2,g7)
    c: Coincident(g1,g6)
    c: Coincident(g2,g4)
    c: Coincident(g0,g6)
    c: Coincident(g0,g4)
FEATURE [App::Part] Board_Geoms_58ce
  Group = -> [Pcb_58ce,PCB_Sketch_58ce]
  Origin = -> Origin
FEATURE [Part::Feature] Shape  label="D24_D_SOD_123_0f779e6ff9e7"
  Placement = pos=(3.66673,13.8333,0) rot=(0,0,-1;0.785398rad)
  shape: bbox 3.147 x 3.147 x 1.25 mm, 67 faces (baked)
FEATURE [Part::Feature] Shape001  label="J4_SOLID_42e36dcc9d63"
  Placement = pos=(10.9645,42.4,0) rot=(0,0.707107,0.707107;3.14159rad)
  shape: bbox 5.501 x 4.001 x 0.9009 mm, 979 faces (baked)
FEATURE [App::Link] D24_D_SOD_123_0f779e6ff9e7_ln_  label="D23_D_SOD_123_3fd67df90355"
  LinkPlacement = pos=(5.66673,15.8333,0) rot=(0,0,-1;0.785398rad)
  LinkedObject = -> Shape
  Placement = pos=(5.66673,15.8333,0) rot=(0,0,-1;0.785398rad)
FEATURE [App::Link] D24_D_SOD_123_0f779e6ff9e7_ln_001  label="D30_D_SOD_123_61e72e2af53f"
  LinkPlacement = pos=(19.75,16.55,0) rot=(0,0,-1;1.5708rad)
  LinkedObject = -> Shape
  Placement = pos=(19.75,16.55,0) rot=(0,0,-1;1.5708rad)
FEATURE [App::Link] D24_D_SOD_123_0f779e6ff9e7_ln_002  label="D27_D_SOD_123_7b2efe9b5669"
  LinkPlacement = pos=(17.6667,24.3333,0) rot=(0,0,1;2.35619rad)
  LinkedObject = -> Shape
  Placement = pos=(17.6667,24.3333,0) rot=(0,0,1;2.35619rad)
FEATURE [App::Link] D24_D_SOD_123_0f779e6ff9e7_ln_003  label="D22_D_SOD_123_057a97edfa83"
  LinkPlacement = pos=(7.66673,17.8333,0) rot=(0,0,-1;0.785398rad)
  LinkedObject = -> Shape
  Placement = pos=(7.66673,17.8333,0) rot=(0,0,-1;0.785398rad)
FEATURE [App::Link] D24_D_SOD_123_0f779e6ff9e7_ln_004  label="D29_D_SOD_123_cdf521000048"
  LinkPlacement = pos=(16.5,16.55,0) rot=(0,0,-1;1.5708rad)
  LinkedObject = -> Shape
  Placement = pos=(16.5,16.55,0) rot=(0,0,-1;1.5708rad)
FEATURE [App::Link] D24_D_SOD_123_0f779e6ff9e7_ln_005  label="D28_D_SOD_123_d5d7d507dfc1"
  LinkPlacement = pos=(15.6667,22.3333,0) rot=(0,0,1;2.35619rad)
  LinkedObject = -> Shape
  Placement = pos=(15.6667,22.3333,0) rot=(0,0,1;2.35619rad)
FEATURE [App::Link] D24_D_SOD_123_0f779e6ff9e7_ln_006  label="D20_D_SOD_123_675b5f77a9ad"
  LinkPlacement = pos=(5.16673,33.8333,0) rot=(0,0,-1;0.785398rad)
  LinkedObject = -> Shape
  Placement = pos=(5.16673,33.8333,0) rot=(0,0,-1;0.785398rad)
FEATURE [Part::Feature] Part__Feature  label="SKRHAD"
  shape: bbox 7.483 x 7.5 x 5.5 mm, 242 faces (baked)
FEATURE [Part::Feature] Part__Feature001  label="Pins"
  shape: bbox 1.15 x 0.8 x 0.1 mm, 6 faces (baked)
FEATURE [Part::Feature] Part__Feature002  label="Pins001"
  shape: bbox 1.15 x 0.8 x 0.1 mm, 6 faces (baked)
FEATURE [Part::Feature] Part__Feature003  label="Pins002"
  shape: bbox 1.15 x 0.8 x 0.1 mm, 6 faces (baked)
FEATURE [Part::Feature] Part__Feature004  label="Pins003"
  shape: bbox 1.15 x 0.8 x 0.1 mm, 6 faces (baked)
FEATURE [Part::Feature] Part__Feature005  label="Pins004"
  shape: bbox 1.15 x 0.8 x 0.1 mm, 6 faces (baked)
FEATURE [Part::Feature] Part__Feature006  label="Pins005"
  shape: bbox 1.15 x 0.8 x 0.1 mm, 6 faces (baked)
FEATURE [Part::Feature] Part__Feature007  label="Pins006"
  shape: bbox 1.64 x 1.44 x 0.1 mm, 6 faces (baked)
FEATURE [Part::Feature] Part__Feature008  label="Pins007"
  shape: bbox 1.64 x 1.44 x 0.1 mm, 6 faces (baked)
FEATURE [Part::Feature] Part__Feature009  label="Lugs"
  shape: bbox 0.55 x 0.55 x 1.8 mm, 3 faces (baked)
FEATURE [Part::Feature] Part__Feature010  label="Lugs001"
  shape: bbox 0.85 x 0.85 x 1.8 mm, 3 faces (baked)
FEATURE [App::Part] SKRHADE  label="S6_SKRHADE_66ce9957abdd"
  Group = -> [Part__Feature,Part__Feature001,Part__Feature002,Part__Feature003,Part__Feature004,Part__Feature005,Part__Feature006,Part__Feature007,Part__Feature008,Part__Feature009,Part__Feature010]
  Origin = -> Origin008
  Placement = pos=(10.9645,9.96447,0) rot=(0,0,-1;0.785398rad)
FEATURE [App::Link] D24_D_SOD_123_0f779e6ff9e7_ln_007  label="D21_D_SOD_123_014bcfdeeddd"
  LinkPlacement = pos=(3.16673,31.8333,0) rot=(0,0,-1;0.785398rad)
  LinkedObject = -> Shape
  Placement = pos=(3.16673,31.8333,0) rot=(0,0,-1;0.785398rad)
FEATURE [App::Link] D24_D_SOD_123_0f779e6ff9e7_ln_008  label="D19_D_SOD_123_2a26592c9c0c"
  LinkPlacement = pos=(7.16673,35.8333,0) rot=(0,0,-1;0.785398rad)
  LinkedObject = -> Shape
  Placement = pos=(7.16673,35.8333,0) rot=(0,0,-1;0.785398rad)
FEATURE [App::Link] S6_SKRHADE_66ce9957abdd_ln_  label="S5_SKRHADE_e4e283c67a98"
  LinkPlacement = pos=(10.9645,28.5203,0) rot=(0,0,-1;0.785398rad)
  LinkedObject = -> SKRHADE
  Placement = pos=(10.9645,28.5203,0) rot=(0,0,-1;0.785398rad)
FEATURE [App::Part] Top_58ce
  Group = -> [Shape,Shape001,D24_D_SOD_123_0f779e6ff9e7_ln_,D24_D_SOD_123_0f779e6ff9e7_ln_001,D24_D_SOD_123_0f779e6ff9e7_ln_002,D24_D_SOD_123_0f779e6ff9e7_ln_003,D24_D_SOD_123_0f779e6ff9e7_ln_004,D24_D_SOD_123_0f779e6ff9e7_ln_005,D24_D_SOD_123_0f779e6ff9e7_ln_006,SKRHADE,D24_D_SOD_123_0f779e6ff9e7_ln_007,D24_D_SOD_123_0f779e6ff9e7_ln_008,S6_SKRHADE_66ce9957abdd_ln_]
  Origin = -> Origin003
FEATURE [App::Part] Step_Models_58ce
  Group = -> [Top_58ce]
  Origin = -> Origin002
FEATURE [Sketcher::SketchObject] Sketch  label="2.2"
  ArcFitTolerance = 1e-06
  FullyConstrained = false
  MakeInternals = false
  Placement = pos=(0,0,0) rot=(0,0,1;3.14159rad)
  sketch-geometry (8):
    g0: LineSegment StartX=-23.2 StartY=-44 StartZ=0 EndX=-23.2 EndY=-0.999999 EndZ=0
    g1: ArcOfCircle CenterX=-20 CenterY=-0.999999 CenterZ=0 NormalX=0 NormalY=0 NormalZ=1 AngleXU=-3.14159 Radius=3.2 StartAngle=4.71239 EndAngle=6.28318
    g2: LineSegment StartX=-20 StartY=2.2 StartZ=0 EndX=-0.999999 EndY=2.2 EndZ=0
    g3: ArcOfCircle CenterX=-0.999999 CenterY=-0.999999 CenterZ=0 NormalX=0 NormalY=0 NormalZ=1 AngleXU=1.5708 Radius=3.2 StartAngle=4.71239 EndAngle=6.28318
    g4: LineSegment StartX=2.2 StartY=-0.999999 StartZ=0 EndX=2.2 EndY=-44 EndZ=0
    g5: ArcOfCircle CenterX=-0.999999 CenterY=-44 CenterZ=0 NormalX=0 NormalY=0 NormalZ=1 AngleXU=7.47076e-07 Radius=3.2 StartAngle=4.71239 EndAngle=6.28318
    g6: LineSegment StartX=-0.999999 StartY=-47.2 StartZ=0 EndX=-20 EndY=-47.2 EndZ=0
    g7: ArcOfCircle CenterX=-20 CenterY=-44 CenterZ=0 NormalX=0 NormalY=0 NormalZ=1 AngleXU=-1.5708 Radius=3.2 StartAngle=4.71239 EndAngle=6.28318
  constraints (12):
    c: Vertical(g0)
    c: Coincident(g0,g1)
    c: Coincident(g1,g2)
    c: Horizontal(g2)
    c: Coincident(g2,g3)
    c: Coincident(g3,g4)
    c: Vertical(g4)
    c: Coincident(g4,g5)
    c: Coincident(g5,g6)
    c: Horizontal(g6)
    c: Coincident(g6,g7)
    c: Coincident(g7,g0)
FEATURE [Sketcher::SketchObject] Sketch025  label="2.003"
  ArcFitTolerance = 1e-06
  FullyConstrained = false
  MakeInternals = false
  Placement = pos=(0,0,0) rot=(0,0,1;3.14159rad)
  sketch-geometry (8):
    g0: LineSegment StartX=-23.4 StartY=-44 StartZ=0 EndX=-23.4 EndY=-0.999999 EndZ=0
    g1: ArcOfCircle CenterX=-20 CenterY=-0.999999 CenterZ=0 NormalX=0 NormalY=0 NormalZ=1 AngleXU=0 Radius=3.4 StartAngle=1.5708 EndAngle=3.14159
    g2: LineSegment StartX=-20 StartY=2.4 StartZ=0 EndX=-0.999999 EndY=2.4 EndZ=0
    g3: ArcOfCircle CenterX=-0.999999 CenterY=-0.999999 CenterZ=0 NormalX=0 NormalY=0 NormalZ=1 AngleXU=0 Radius=3.4 StartAngle=6.28318 EndAngle=7.85398
    g4: LineSegment StartX=2.4 StartY=-1 StartZ=0 EndX=2.4 EndY=-44 EndZ=0
    g5: ArcOfCircle CenterX=-0.999999 CenterY=-44 CenterZ=0 NormalX=0 NormalY=0 NormalZ=1 AngleXU=0 Radius=3.4 StartAngle=4.71239 EndAngle=6.28318
    g6: LineSegment StartX=-0.999999 StartY=-47.4 StartZ=0 EndX=-20 EndY=-47.4 EndZ=0
    g7: ArcOfCircle CenterX=-20 CenterY=-44 CenterZ=0 NormalX=0 NormalY=0 NormalZ=1 AngleXU=0 Radius=3.4 StartAngle=3.14159 EndAngle=4.71239
  constraints (12):
    c: Vertical(g0)
    c: Coincident(g0,g1)
    c: Coincident(g1,g2)
    c: Horizontal(g2)
    c: Coincident(g2,g3)
    c: Coincident(g3,g4)
    c: Vertical(g4)
    c: Coincident(g4,g5)
    c: Coincident(g5,g6)
    c: Horizontal(g6)
    c: Coincident(g6,g7)
    c: Coincident(g7,g0)
FEATURE [PartDesign::Pad] Pad
  Direction = (0,0,1)
  Length = 3.2
  Length2 = 10
  Placement = pos=(0,0,0) rot=(0,0,1;3.14159rad)
  Profile = -> Sketch025
  ReferenceAxis = -> Sketch025 [N_Axis]
  Refine = true
  Suppressed = false
  Type = 0
FEATURE [PartDesign::Thickness] Thickness
  Base = -> Pad [Face10]
  BaseFeature = -> Pad
  Intersection = false
  Join = 0
  Mode = 0
  Refine = true
  Reversed = true
  SupportTransform = false
  Suppressed = false
  Value = 2
FEATURE [PartDesign::ShapeBinder] ShapeBinder
  Support = -> [Pcb_58ce]
  TraceSupport = false
FEATURE [Sketcher::SketchObject] Sketch026
  ArcFitTolerance = 1e-06
  AttachmentSupport = -> [Thickness]
  ExternalGeometry = -> [ShapeBinder]
  FullyConstrained = true
  MakeInternals = false
  MapMode = 5
  Placement = pos=(0,0,0) rot=(1,0,0;3.14159rad)
  sketch-geometry (4):
    g0: Circle CenterX=3 CenterY=-3 CenterZ=0 NormalX=0 NormalY=0 NormalZ=1 AngleXU=0 Radius=1.25
    g1: Circle CenterX=18 CenterY=-3 CenterZ=0 NormalX=0 NormalY=0 NormalZ=1 AngleXU=0 Radius=1.25
    g2: Circle CenterX=18 CenterY=-42 CenterZ=0 NormalX=0 NormalY=0 NormalZ=1 AngleXU=0 Radius=1.25
    g3: Circle CenterX=3 CenterY=-42 CenterZ=0 NormalX=0 NormalY=0 NormalZ=1 AngleXU=0 Radius=1.25
  constraints (8):
    c: Coincident(g0,g-3)
    c: Coincident(g1,g-4)
    c: Coincident(g2,g-5)
    c: Diameter(g2) = 2.5
    c: Equal(g0,g1)
    c: Equal(g1,g2)
    c: Coincident(g3,g-6)
    c: Equal(g2,g3)
FEATURE [PartDesign::Pocket] Pocket010
  BaseFeature = -> Thickness
  Direction = (0,0,1)
  Length = 5
  Length2 = 5
  Profile = -> Sketch026
  ReferenceAxis = -> Sketch026 [N_Axis]
  Refine = true
  Suppressed = false
  Type = 1
FEATURE [PartDesign::Chamfer] Chamfer001
  Angle = 60
  Base = -> Pocket010 [Edge18,Edge19,Edge16,Edge17]
  BaseFeature = -> Pocket010
  ChamferType = 2
  FlipDirection = false
  Refine = true
  Size = 0.8
  Size2 = 1
  SupportTransform = false
  Suppressed = false
  UseAllEdges = false
FEATURE [PartDesign::Body] Body010  label="base"
  AllowCompound = false
  Group = -> [Sketch025,Pad,Thickness,ShapeBinder,Sketch026,Pocket010,Chamfer001]
  Origin = -> Origin022
  Placement = pos=(0,0,-3.6) rot=(0,0,1;0rad)
  Tip = -> Chamfer001
FEATURE [Sketcher::SketchObject] Sketch027  label="2.004"
  ArcFitTolerance = 1e-06
  FullyConstrained = false
  MakeInternals = false
  Placement = pos=(0,0,0) rot=(0,0,1;3.14159rad)
  sketch-geometry (8):
    g0: LineSegment StartX=-23.4 StartY=-44 StartZ=0 EndX=-23.4 EndY=-1 EndZ=0
    g1: ArcOfCircle CenterX=-20 CenterY=-0.999999 CenterZ=0 NormalX=0 NormalY=0 NormalZ=1 AngleXU=0 Radius=3.4 StartAngle=1.5708 EndAngle=3.14159
    g2: LineSegment StartX=-20 StartY=2.4 StartZ=0 EndX=-1 EndY=2.4 EndZ=0
    g3: ArcOfCircle CenterX=-0.999999 CenterY=-0.999999 CenterZ=0 NormalX=0 NormalY=0 NormalZ=1 AngleXU=0 Radius=3.4 StartAngle=6.28318 EndAngle=7.85398
    g4: LineSegment StartX=2.4 StartY=-1 StartZ=0 EndX=2.4 EndY=-44 EndZ=0
    g5: ArcOfCircle CenterX=-0.999999 CenterY=-44 CenterZ=0 NormalX=0 NormalY=0 NormalZ=1 AngleXU=0 Radius=3.4 StartAngle=4.71239 EndAngle=6.28319
    g6: LineSegment StartX=-0.999999 StartY=-47.4 StartZ=0 EndX=-20 EndY=-47.4 EndZ=0
    g7: ArcOfCircle CenterX=-20 CenterY=-44 CenterZ=0 NormalX=0 NormalY=0 NormalZ=1 AngleXU=0 Radius=3.4 StartAngle=3.14159 EndAngle=4.71239
  constraints (12):
    c: Vertical(g0)
    c: Coincident(g0,g1)
    c: Coincident(g1,g2)
    c: Horizontal(g2)
    c: Coincident(g2,g3)
    c: Coincident(g3,g4)
    c: Vertical(g4)
    c: Coincident(g4,g5)
    c: Coincident(g5,g6)
    c: Horizontal(g6)
    c: Coincident(g6,g7)
    c: Coincident(g7,g0)
FEATURE [PartDesign::Pad] Pad014
  Direction = (0,0,1)
  Length = 5
  Length2 = 10
  Placement = pos=(0,0,0) rot=(0,0,1;3.14159rad)
  Profile = -> Sketch027
  ReferenceAxis = -> Sketch027 [N_Axis]
  Refine = true
  Suppressed = false
  Type = 0
FEATURE [PartDesign::Thickness] Thickness001
  Base = -> Pad014 [Face9]
  BaseFeature = -> Pad014
  Intersection = false
  Join = 0
  Mode = 0
  Refine = true
  Reversed = true
  SupportTransform = false
  Suppressed = false
  Value = 2
FEATURE [PartDesign::SubShapeBinder] Binder001
  BindCopyOnChange = 0
  BindMode = 0
  ClaimChildren = false
  Context = -> Board_58ce [Part001.Body011.Binder001.]
  Fuse = false
  MakeFace = true
  OffsetFill = false
  OffsetIntersection = false
  OffsetJoinType = 0
  OffsetOpenResult = false
  PartialLoad = false
  Refine = true
  Relative = true
  Support = -> [Step_Models_58ce[Top_58ce.S6_SKRHADE_66ce9957abdd_ln_.Part__Feature.Edge656,Top_58ce.S6_SKRHADE_66ce9957abdd_ln_.Part__Feature.Edge660,Top_58ce.SKRHADE.Part__Feature.Edge656,Top_58ce.SKRHADE.Part__Feature.Edge660]]
  _Version = 2
FEATURE [Sketcher::SketchObject] Sketch029
  ArcFitTolerance = 1e-06
  AttachmentSupport = -> [Thickness001]
  ExternalGeometry = -> [Binder001]
  FullyConstrained = false
  MakeInternals = false
  MapMode = 5
  Placement = pos=(0,0,5) rot=(0,0,1;0rad)
  sketch-geometry (6):
    g0: LineSegment [constr] StartX=11.8395 StartY=28.5203 StartZ=0 EndX=10.4199 EndY=28.5203 EndZ=0
    g1: LineSegment [constr] StartX=10.9645 StartY=27.6453 StartZ=0 EndX=10.9645 EndY=28.5203 EndZ=0
    g2: LineSegment [constr] StartX=11.8395 StartY=9.96447 StartZ=0 EndX=10.2544 EndY=9.96447 EndZ=0
    g3: LineSegment [constr] StartX=10.9645 StartY=9.08947 StartZ=0 EndX=10.9645 EndY=9.96447 EndZ=0
    g4: Circle CenterX=10.9645 CenterY=9.96447 CenterZ=0 NormalX=0 NormalY=0 NormalZ=1 AngleXU=0 Radius=4.5
    g5: Circle CenterX=10.9645 CenterY=28.5203 CenterZ=0 NormalX=0 NormalY=0 NormalZ=1 AngleXU=0 Radius=4.5
  constraints (14):
    c: Symmetric(g-4,g-4,g0)
    c: Horizontal(g0)
    c: Symmetric(g-3,g-3,g1)
    c: PointOnObject(g1,g0)
    c: Vertical(g1)
    c: Symmetric(g-6,g-6,g2)
    c: Horizontal(g2)
    c: Symmetric(g-5,g-5,g3)
    c: PointOnObject(g3,g2)
    c: Vertical(g3)
    c: Diameter(g4) = 9
    c: Coincident(g4,g3)
    c: Diameter(g5) = 9
    c: Coincident(g5,g1)
FEATURE [PartDesign::Pocket] Pocket011
  BaseFeature = -> Thickness001
  Direction = (0,0,-1)
  Length = 5
  Length2 = 5
  Profile = -> Sketch029
  ReferenceAxis = -> Sketch029 [N_Axis]
  Refine = true
  Suppressed = false
  Type = 1
FEATURE [PartDesign::SubShapeBinder] Binder002
  BindCopyOnChange = 0
  BindMode = 0
  ClaimChildren = false
  Context = -> Board_58ce [Part001.Body011.Binder002.]
  Fuse = false
  MakeFace = true
  OffsetFill = false
  OffsetIntersection = false
  OffsetJoinType = 0
  OffsetOpenResult = false
  PartialLoad = false
  Refine = true
  Relative = true
  Support = -> [Board_Geoms_58ce[Pcb_58ce.Edge35,Pcb_58ce.Edge101,Pcb_58ce.Edge134,Pcb_58ce.Edge71]]
  _Version = 2
FEATURE [Sketcher::SketchObject] Sketch030
  ArcFitTolerance = 1e-06
  AttachmentSupport = -> [Pocket011]
  ExternalGeometry = -> [Binder002]
  FullyConstrained = true
  MakeInternals = false
  MapMode = 5
  Placement = pos=(0,0,0) rot=(1,0,0;3.14159rad)
  sketch-geometry (4):
    g0: Circle CenterX=3 CenterY=-3 CenterZ=0 NormalX=0 NormalY=0 NormalZ=1 AngleXU=0 Radius=3
    g1: Circle CenterX=18 CenterY=-3 CenterZ=0 NormalX=0 NormalY=0 NormalZ=1 AngleXU=0 Radius=3
    g2: Circle CenterX=18 CenterY=-42 CenterZ=0 NormalX=0 NormalY=0 NormalZ=1 AngleXU=0 Radius=3
    g3: Circle CenterX=3 CenterY=-42 CenterZ=0 NormalX=0 NormalY=0 NormalZ=1 AngleXU=0 Radius=3
  constraints (8):
    c: Diameter(g0) = 6
    c: Coincident(g0,g-3)
    c: Diameter(g1) = 6
    c: Coincident(g1,g-4)
    c: Diameter(g2) = 6
    c: Coincident(g2,g-5)
    c: Diameter(g3) = 6
    c: Coincident(g3,g-6)
FEATURE [PartDesign::Pad] Pad015
  BaseFeature = -> Pocket011
  Direction = (0,0,-1)
  Length = 10
  Length2 = 10
  Profile = -> Sketch030
  ReferenceAxis = -> Sketch030 [N_Axis]
  Refine = true
  Suppressed = false
  Type = 3
  UpToFace = -> Pocket011 [Face21]
FEATURE [Sketcher::SketchObject] Sketch031
  ArcFitTolerance = 1e-06
  AttachmentSupport = -> [Pad015]
  ExternalGeometry = -> [Pad015]
  FullyConstrained = true
  MakeInternals = false
  MapMode = 5
  Placement = pos=(0,0,0) rot=(1,0,0;3.14159rad)
  sketch-geometry (4):
    g0: Circle CenterX=3 CenterY=-3 CenterZ=0 NormalX=0 NormalY=0 NormalZ=1 AngleXU=0 Radius=1.65
    g1: Circle CenterX=18 CenterY=-3 CenterZ=0 NormalX=0 NormalY=0 NormalZ=1 AngleXU=0 Radius=1.65
    g2: Circle CenterX=18 CenterY=-42 CenterZ=0 NormalX=0 NormalY=0 NormalZ=1 AngleXU=0 Radius=1.65
    g3: Circle CenterX=3 CenterY=-42 CenterZ=0 NormalX=0 NormalY=0 NormalZ=1 AngleXU=0 Radius=1.65
  constraints (8):
    c: Diameter(g0) = 3.3
    c: Coincident(g0,g-3)
    c: Diameter(g1) = 3.3
    c: Coincident(g1,g-4)
    c: Diameter(g2) = 3.3
    c: Coincident(g2,g-5)
    c: Diameter(g3) = 3.3
    c: Coincident(g3,g-6)
FEATURE [PartDesign::Pocket] Pocket012
  BaseFeature = -> Pad015
  Direction = (0,0,1)
  Length = 3.3
  Length2 = 5
  Profile = -> Sketch031
  ReferenceAxis = -> Sketch031 [N_Axis]
  Refine = true
  Suppressed = false
  Type = 0
FEATURE [Sketcher::SketchObject] Sketch032
  ArcFitTolerance = 1e-06
  FullyConstrained = false
  MakeInternals = false
  Placement = pos=(0,0,0) rot=(0,0,1;3.14159rad)
  sketch-geometry (8):
    g0: LineSegment StartX=-23.4 StartY=-44 StartZ=0 EndX=-23.4 EndY=-0.999999 EndZ=0
    g1: ArcOfCircle CenterX=-20 CenterY=-0.999999 CenterZ=0 NormalX=0 NormalY=0 NormalZ=1 AngleXU=-3.14159 Radius=3.4 StartAngle=4.71239 EndAngle=6.28318
    g2: LineSegment StartX=-20 StartY=2.4 StartZ=0 EndX=-0.999999 EndY=2.4 EndZ=0
    g3: ArcOfCircle CenterX=-0.999999 CenterY=-0.999999 CenterZ=0 NormalX=0 NormalY=0 NormalZ=1 AngleXU=1.5708 Radius=3.4 StartAngle=4.71239 EndAngle=6.28318
    g4: LineSegment StartX=2.4 StartY=-0.999999 StartZ=0 EndX=2.4 EndY=-44 EndZ=0
    g5: ArcOfCircle CenterX=-0.999999 CenterY=-44 CenterZ=0 NormalX=0 NormalY=0 NormalZ=1 AngleXU=7.47076e-07 Radius=3.4 StartAngle=4.71239 EndAngle=6.28318
    g6: LineSegment StartX=-0.999999 StartY=-47.4 StartZ=0 EndX=-20 EndY=-47.4 EndZ=0
    g7: ArcOfCircle CenterX=-20 CenterY=-44 CenterZ=0 NormalX=0 NormalY=0 NormalZ=1 AngleXU=-1.5708 Radius=3.4 StartAngle=4.71239 EndAngle=6.28318
  constraints (12):
    c: Vertical(g0)
    c: Coincident(g0,g1)
    c: Coincident(g1,g2)
    c: Horizontal(g2)
    c: Coincident(g2,g3)
    c: Coincident(g3,g4)
    c: Vertical(g4)
    c: Coincident(g4,g5)
    c: Coincident(g5,g6)
    c: Horizontal(g6)
    c: Coincident(g6,g7)
    c: Coincident(g7,g0)
FEATURE [Sketcher::SketchObject] Sketch033
  ArcFitTolerance = 1e-06
  AttachmentSupport = -> [Pocket012]
  ExternalGeometry = -> [Pocket012]
  FullyConstrained = false
  MakeInternals = false
  MapMode = 5
  Placement = pos=(0,47.4,0) rot=(0,0.707107,0.707107;3.14159rad)
  sketch-geometry (8):
    g0: LineSegment StartX=-14.6619 StartY=0 StartZ=0 EndX=-7.26206 EndY=0 EndZ=0
    g1: LineSegment StartX=-7.26206 StartY=0 StartZ=0 EndX=-7.26206 EndY=1.78706 EndZ=0
    g2: LineSegment StartX=-7.55642 StartY=2.08141 StartZ=0 EndX=-14.3676 EndY=2.08141 EndZ=0
    g3: LineSegment StartX=-14.6619 StartY=1.78706 StartZ=0 EndX=-14.6619 EndY=0 EndZ=0
    g4: ArcOfCircle CenterX=-14.3676 CenterY=1.78706 CenterZ=0 NormalX=0 NormalY=0 NormalZ=1 AngleXU=0 Radius=0.294356 StartAngle=1.5708 EndAngle=3.14159
    g5: GeomPoint [constr] X=-14.6619 Y=2.08141 Z=0
    g6: ArcOfCircle CenterX=-7.55642 CenterY=1.78706 CenterZ=0 NormalX=0 NormalY=0 NormalZ=1 AngleXU=0 Radius=0.294356 StartAngle=0 EndAngle=1.5708
    g7: GeomPoint [constr] X=-7.26206 Y=2.08141 Z=0
  constraints (15):
    c: Coincident(g0,g1)
    c: Coincident(g3,g0)
    c: Horizontal(g0)
    c: Horizontal(g2)
    c: Vertical(g1)
    c: Vertical(g3)
    c: PointOnObject(g0,g-3)
    c: PointOnObject(g5,g2)
    c: PointOnObject(g5,g3)
    c: Tangent(g2,g4) = -1.5708
    c: Tangent(g3,g4) = -1.5708
    c: PointOnObject(g7,g1)
    c: PointOnObject(g7,g2)
    c: Tangent(g1,g6) = -1.5708
    c: Tangent(g2,g6) = -1.5708
FEATURE [PartDesign::Pocket] Pocket
  BaseFeature = -> Pocket012
  Direction = (0,-1,2e-16)
  Length = 2
  Length2 = 5
  Profile = -> Sketch033
  ReferenceAxis = -> Sketch033 [N_Axis]
  Refine = true
  Suppressed = false
  Type = 0
FEATURE [PartDesign::Chamfer] Chamfer
  Angle = 45
  Base = -> Pocket [Edge34,Edge33]
  BaseFeature = -> Pocket
  ChamferType = 0
  FlipDirection = false
  Refine = true
  Size = 1
  Size2 = 1
  SupportTransform = false
  Suppressed = false
  UseAllEdges = false
FEATURE [PartDesign::Chamfer] Chamfer002
  Angle = 45
  Base = -> Chamfer [Edge5]
  BaseFeature = -> Chamfer
  ChamferType = 0
  FlipDirection = false
  Refine = true
  Size = 1.5
  Size2 = 1
  SupportTransform = false
  Suppressed = false
  UseAllEdges = false
FEATURE [PartDesign::Body] Body011  label="top"
  AllowCompound = false
  Group = -> [Sketch027,Pad014,Thickness001,Binder001,Sketch029,Pocket011,Binder002,Sketch030,Pad015,Sketch031,Pocket012,Sketch033,Pocket,Chamfer,Chamfer002]
  Origin = -> Origin023
  Tip = -> Chamfer002
FEATURE [App::Part] Part001  label="case"
  Group = -> [Body010,Body011]
  Origin = -> Origin021
FEATURE [App::Part] Board_58ce  label="thumb-cluster"
  Group = -> [Local_CS_58ce,Board_Geoms_58ce,Step_Models_58ce,Part001]
  Origin = -> Origin001
---- part thumbstick-breakout.FCStd = doc fcstd_39c8789a8ab7 ----
FCSTD DOCUMENT  (FreeCAD 1.0RUnknown)
Label: thumbstick-breakout
License: All rights reserved
LicenseURL: https://en.wikipedia.org/wiki/All_rights_reserved
objects: Sketcher::SketchObject×14, App::Part×6, PartDesign::Pad×6, PartDesign::ShapeBinder×5, PartDesign::Pocket×5, PartDesign::Body×4, Part::Feature×3, PartDesign::Thickness×2, PartDesign::CoordinateSystem×1, Part::Ellipsoid×1, PartDesign::Plane×1, PartDesign::Chamfer×1, PartDesign::Revolution×1
note: 88 computed .brp shape members not serialized (recipe doc carries the construction recipe); baked Part::Feature solids carry a one-line shape summary decoded from their .brp

FEATURE [PartDesign::CoordinateSystem] Local_CS_bbd4
  AttacherType = Attacher::AttachEngine3D
  MapMode = 2
FEATURE [Part::Feature] Pcb_bbd4
  Placement = pos=(-137.3,117.78,0) rot=(0,0,1;0rad)
  shape: bbox 25.4 x 31.75 x 1.6 mm, 24 faces (baked)
FEATURE [Sketcher::SketchObject] PCB_Sketch_bbd4
  ArcFitTolerance = 1e-06
  FullyConstrained = false
  MakeInternals = false
  sketch-geometry (4):
    g0: LineSegment StartX=0 StartY=31.75 StartZ=0 EndX=0 EndY=0 EndZ=0
    g1: LineSegment StartX=25.4 StartY=31.75 StartZ=0 EndX=0 EndY=31.75 EndZ=0
    g2: LineSegment StartX=0 StartY=0 StartZ=0 EndX=25.4 EndY=0 EndZ=0
    g3: LineSegment StartX=25.4 StartY=0 StartZ=0 EndX=25.4 EndY=31.75 EndZ=0
  constraints (4):
    c: Coincident(g0,g2)
    c: Coincident(g0,g1)
    c: Coincident(g2,g3)
    c: Coincident(g1,g3)
FEATURE [App::Part] Board_Geoms_bbd4
  Group = -> [Pcb_bbd4,PCB_Sketch_bbd4]
  Origin = -> Origin
FEATURE [Part::Feature] Shape  label="J1_SOLID_4955641dfa02"
  Placement = pos=(12.66,29.4,0) rot=(0,0.707107,0.707107;3.14159rad)
  shape: bbox 4.001 x 3.601 x 0.9007 mm, 670 faces (baked)
FEATURE [App::Part] Top_bbd4
  Group = -> [Shape]
  Origin = -> Origin003
FEATURE [App::Part] Step_Models_bbd4
  Group = -> [Top_bbd4]
  Origin = -> Origin002
FEATURE [App::Part] Board_bbd4  label="thumbstick-breakout"
  Group = -> [Local_CS_bbd4,Board_Geoms_bbd4,Step_Models_bbd4]
  Origin = -> Origin001
FEATURE [Sketcher::SketchObject] Sketch009  label="2.005"
  ArcFitTolerance = 1e-06
  FullyConstrained = false
  MakeInternals = false
  sketch-geometry (8):
    g0: LineSegment StartX=-2.4 StartY=31.75 StartZ=0 EndX=-2.4 EndY=0 EndZ=0
    g1: ArcOfCircle CenterX=4.026e-13 CenterY=0 CenterZ=0 NormalX=0 NormalY=0 NormalZ=1 AngleXU=0 Radius=2.4 StartAngle=3.14159 EndAngle=4.71239
    g2: LineSegment StartX=4.70767e-08 StartY=-2.4 StartZ=0 EndX=25.4 EndY=-2.4 EndZ=0
    g3: ArcOfCircle CenterX=25.4 CenterY=0 CenterZ=0 NormalX=0 NormalY=0 NormalZ=1 AngleXU=0 Radius=2.4 StartAngle=4.71239 EndAngle=6.28318
    g4: LineSegment StartX=27.8 StartY=-7.37231e-07 StartZ=0 EndX=27.8 EndY=31.75 EndZ=0
    g5: ArcOfCircle CenterX=25.4 CenterY=31.75 CenterZ=0 NormalX=0 NormalY=0 NormalZ=1 AngleXU=0 Radius=2.4 StartAngle=0 EndAngle=1.5708
    g6: LineSegment StartX=25.4 StartY=34.15 StartZ=0 EndX=7.84308e-07 EndY=34.15 EndZ=0
    g7: ArcOfCircle CenterX=0 CenterY=31.75 CenterZ=0 NormalX=0 NormalY=0 NormalZ=1 AngleXU=0 Radius=2.4 StartAngle=1.5708 EndAngle=3.14159
  constraints (12):
    c: Vertical(g0)
    c: Coincident(g0,g1)
    c: Coincident(g1,g2)
    c: Horizontal(g2)
    c: Coincident(g2,g3)
    c: Coincident(g3,g4)
    c: Vertical(g4)
    c: Coincident(g4,g5)
    c: Coincident(g5,g6)
    c: Horizontal(g6)
    c: Coincident(g6,g7)
    c: Coincident(g7,g0)
FEATURE [PartDesign::Pad] Pad
  Direction = (0,0,1)
  Length = 3.2
  Length2 = 10
  Profile = -> Sketch009
  ReferenceAxis = -> Sketch009 [N_Axis]
  Refine = true
  Suppressed = false
  Type = 0
FEATURE [PartDesign::Thickness] Thickness001
  Base = -> Pad [Face10]
  BaseFeature = -> Pad
  Intersection = false
  Join = 0
  Mode = 0
  Refine = true
  Reversed = true
  SupportTransform = false
  Suppressed = false
  Value = 2
FEATURE [PartDesign::ShapeBinder] ShapeBinder
  Support = -> [Pcb_bbd4]
  TraceSupport = false
FEATURE [Sketcher::SketchObject] Sketch010
  ArcFitTolerance = 1e-06
  AttachmentSupport = -> [Thickness001]
  ExternalGeometry = -> [ShapeBinder]
  FullyConstrained = true
  MakeInternals = false
  MapMode = 5
  Placement = pos=(0,0,2) rot=(0,0,1;0rad)
  sketch-geometry (4):
    g0: Circle CenterX=2.54 CenterY=29.21 CenterZ=0 NormalX=0 NormalY=0 NormalZ=1 AngleXU=0 Radius=1.25
    g1: Circle CenterX=22.86 CenterY=29.21 CenterZ=0 NormalX=0 NormalY=0 NormalZ=1 AngleXU=0 Radius=1.25
    g2: Circle CenterX=22.86 CenterY=2.54 CenterZ=0 NormalX=0 NormalY=0 NormalZ=1 AngleXU=0 Radius=1.25
    g3: Circle CenterX=2.54 CenterY=2.54 CenterZ=0 NormalX=0 NormalY=0 NormalZ=1 AngleXU=0 Radius=1.25
  constraints (8):
    c: Diameter(g0) = 2.5
    c: Coincident(g0,g-3)
    c: Diameter(g1) = 2.5
    c: Coincident(g1,g-4)
    c: Diameter(g2) = 2.5
    c: Coincident(g2,g-5)
    c: Diameter(g3) = 2.5
    c: Coincident(g3,g-6)
FEATURE [PartDesign::Pocket] Pocket002
  BaseFeature = -> Thickness001
  Direction = (0,0,-1)
  Length = 5
  Length2 = 5
  Profile = -> Sketch010
  ReferenceAxis = -> Sketch010 [N_Axis]
  Refine = true
  Suppressed = false
  Type = 1
FEATURE [PartDesign::ShapeBinder] ShapeBinder003
  Support = -> [Pcb_bbd4]
  TraceSupport = false
FEATURE [Sketcher::SketchObject] Sketch011
  ArcFitTolerance = 1e-06
  AttachmentSupport = -> [Pocket002]
  ExternalGeometry = -> [ShapeBinder003]
  FullyConstrained = true
  MakeInternals = false
  MapMode = 5
  Placement = pos=(0,0,2) rot=(0,0,1;0rad)
  sketch-geometry (14):
    g0: Circle CenterX=9.45 CenterY=24.043 CenterZ=0 NormalX=0 NormalY=0 NormalZ=1 AngleXU=0 Radius=1.5
    g1: Circle CenterX=15.95 CenterY=24.043 CenterZ=0 NormalX=0 NormalY=0 NormalZ=1 AngleXU=0 Radius=1.5
    g2: Circle CenterX=15.95 CenterY=19.543 CenterZ=0 NormalX=0 NormalY=0 NormalZ=1 AngleXU=0 Radius=1.5
    g3: Circle CenterX=19.025 CenterY=18.793 CenterZ=0 NormalX=0 NormalY=0 NormalZ=1 AngleXU=0 Radius=1.5
    g4: Circle CenterX=19.025 CenterY=8.793 CenterZ=0 NormalX=0 NormalY=0 NormalZ=1 AngleXU=0 Radius=1.5
    g5: Circle CenterX=9.45 CenterY=19.543 CenterZ=0 NormalX=0 NormalY=0 NormalZ=1 AngleXU=0 Radius=1.5
    g6: Circle CenterX=6.375 CenterY=18.793 CenterZ=0 NormalX=0 NormalY=0 NormalZ=1 AngleXU=0 Radius=1.5
    g7: Circle CenterX=6.375 CenterY=8.793 CenterZ=0 NormalX=0 NormalY=0 NormalZ=1 AngleXU=0 Radius=1.5
    g8: Circle CenterX=3.97 CenterY=16.293 CenterZ=0 NormalX=0 NormalY=0 NormalZ=1 AngleXU=0 Radius=1.2
    g9: Circle CenterX=3.97 CenterY=13.793 CenterZ=0 NormalX=0 NormalY=0 NormalZ=1 AngleXU=0 Radius=1.2
    g10: Circle CenterX=3.97 CenterY=11.293 CenterZ=0 NormalX=0 NormalY=0 NormalZ=1 AngleXU=0 Radius=1.2
    g11: Circle CenterX=10.2 CenterY=5.063 CenterZ=0 NormalX=0 NormalY=0 NormalZ=1 AngleXU=0 Radius=1.2
    g12: Circle CenterX=12.7 CenterY=5.063 CenterZ=0 NormalX=0 NormalY=0 NormalZ=1 AngleXU=0 Radius=1.2
    g13: Circle CenterX=15.2 CenterY=5.063 CenterZ=0 NormalX=0 NormalY=0 NormalZ=1 AngleXU=0 Radius=1.2
  constraints (28):
    c: Diameter(g0) = 3
    c: Coincident(g0,g-3)
    c: Diameter(g1) = 3
    c: Coincident(g1,g-5)
    c: Diameter(g2) = 3
    c: Coincident(g2,g-6)
    c: Diameter(g3) = 3
    c: Coincident(g3,g-12)
    c: Diameter(g4) = 3
    c: Coincident(g4,g-13)
    c: Diameter(g5) = 3
    c: Coincident(g5,g-4)
    c: Diameter(g6) = 3
    c: Coincident(g6,g-7)
    c: Diameter(g7) = 3
    c: Coincident(g7,g-11)
    c: Diameter(g8) = 2.4
    c: Coincident(g8,g-8)
    c: Diameter(g9) = 2.4
    c: Coincident(g9,g-9)
    c: Diameter(g10) = 2.4
    c: Coincident(g10,g-10)
    c: Diameter(g11) = 2.4
    c: Coincident(g11,g-16)
    c: Diameter(g12) = 2.4
    c: Coincident(g12,g-15)
    c: Diameter(g13) = 2.4
    c: Coincident(g13,g-14)
FEATURE [PartDesign::Pocket] Pocket003
  BaseFeature = -> Pocket002
  Direction = (0,0,-1)
  Length = 1
  Length2 = 5
  Profile = -> Sketch011
  ReferenceAxis = -> Sketch011 [N_Axis]
  Refine = true
  Suppressed = false
  Type = 0
FEATURE [PartDesign::Body] Body  label="base"
  AllowCompound = false
  Group = -> [Sketch009,Pad,Thickness001,ShapeBinder,Sketch010,Pocket002,ShapeBinder003,Sketch011,Pocket003]
  Origin = -> Origin010
  Placement = pos=(0,0,-3.6) rot=(0,0,1;0rad)
  Tip = -> Pocket003
FEATURE [PartDesign::ShapeBinder] ShapeBinder004
  Placement = pos=(-137.3,117.78,0) rot=(0,0,1;0rad)
  Support = -> [Pcb_bbd4]
  TraceSupport = false
FEATURE [Sketcher::SketchObject] Sketch012
  ArcFitTolerance = 1e-06
  AttachmentSupport = -> [ShapeBinder004]
  ExternalGeometry = -> [ShapeBinder004]
  FullyConstrained = false
  MakeInternals = false
  MapMode = 5
  Placement = pos=(-137.3,117.78,0) rot=(0,0,1;0rad)
  sketch-geometry (15):
    g0: Circle CenterX=146.75 CenterY=-93.737 CenterZ=0 NormalX=0 NormalY=0 NormalZ=1 AngleXU=0 Radius=0.2
    g1: Circle CenterX=153.25 CenterY=-93.737 CenterZ=0 NormalX=0 NormalY=0 NormalZ=1 AngleXU=0 Radius=0.2
    g2: Circle CenterX=153.25 CenterY=-98.237 CenterZ=0 NormalX=0 NormalY=0 NormalZ=1 AngleXU=0 Radius=0.2
    g3: Circle CenterX=156.325 CenterY=-98.987 CenterZ=0 NormalX=0 NormalY=0 NormalZ=1 AngleXU=0 Radius=0.2
    g4: Circle CenterX=146.75 CenterY=-98.237 CenterZ=0 NormalX=0 NormalY=0 NormalZ=1 AngleXU=0 Radius=0.2
    g5: Circle CenterX=143.675 CenterY=-98.987 CenterZ=0 NormalX=0 NormalY=0 NormalZ=1 AngleXU=0 Radius=0.2
    g6: Circle CenterX=141.27 CenterY=-101.487 CenterZ=0 NormalX=0 NormalY=0 NormalZ=1 AngleXU=0 Radius=0.2
    g7: Circle CenterX=141.27 CenterY=-103.987 CenterZ=0 NormalX=0 NormalY=0 NormalZ=1 AngleXU=0 Radius=0.2
    g8: Circle CenterX=141.27 CenterY=-106.487 CenterZ=0 NormalX=0 NormalY=0 NormalZ=1 AngleXU=0 Radius=0.2
    g9: Circle CenterX=143.675 CenterY=-108.987 CenterZ=0 NormalX=0 NormalY=0 NormalZ=1 AngleXU=0 Radius=0.2
    g10: Circle CenterX=147.5 CenterY=-112.717 CenterZ=0 NormalX=0 NormalY=0 NormalZ=1 AngleXU=0 Radius=0.2
    g11: Circle CenterX=150 CenterY=-112.717 CenterZ=0 NormalX=0 NormalY=0 NormalZ=1 AngleXU=0 Radius=0.2
    g12: Circle CenterX=152.5 CenterY=-112.717 CenterZ=0 NormalX=0 NormalY=0 NormalZ=1 AngleXU=0 Radius=0.2
    g13: Circle CenterX=152.599 CenterY=-112.925 CenterZ=0 NormalX=0 NormalY=0 NormalZ=1 AngleXU=0 Radius=0.2
    g14: Circle CenterX=156.325 CenterY=-108.987 CenterZ=0 NormalX=0 NormalY=0 NormalZ=1 AngleXU=0 Radius=0.2
  constraints (15):
    c: Coincident(g0,g-3)
    c: Coincident(g1,g-4)
    c: Coincident(g2,g-5)
    c: Coincident(g3,g-6)
    c: Coincident(g4,g-7)
    c: Coincident(g5,g-8)
    c: Coincident(g6,g-9)
    c: Coincident(g7,g-10)
    c: Coincident(g8,g-11)
    c: Coincident(g9,g-12)
    c: Coincident(g10,g-13)
    c: Coincident(g11,g-14)
    c: Coincident(g14,g-16)
    c: Equal(g0, g1-g14) x14
    c: Radius(g0) = 0.2
FEATURE [Sketcher::SketchObject] Sketch013
  ArcFitTolerance = 1e-06
  AttachmentSupport = -> [XY_Plane012]
  ExternalGeometry = -> [ShapeBinder004]
  FullyConstrained = false
  MakeInternals = false
  MapMode = 5
  sketch-geometry (14):
    g0: LineSegment StartX=17.3886 StartY=25.1014 StartZ=0 EndX=8.04245 EndY=25.1014 EndZ=0
    g1: LineSegment StartX=6.375 StartY=18.793 StartZ=0 EndX=2.6831 EndY=18.793 EndZ=0
    g2: LineSegment StartX=2.6831 StartY=18.793 StartZ=0 EndX=2.6831 EndY=8.793 EndZ=0
    g3: LineSegment StartX=2.6831 StartY=8.793 StartZ=0 EndX=6.375 EndY=8.793 EndZ=0
    g4: LineSegment StartX=8.26567 StartY=4.26908 StartZ=0 EndX=16.6861 EndY=4.26908 EndZ=0
    g5: LineSegment StartX=16.6861 StartY=4.26908 StartZ=0 EndX=16.6861 EndY=8.793 EndZ=0
    g6: LineSegment StartX=16.6861 StartY=8.793 StartZ=0 EndX=19.025 EndY=8.793 EndZ=0
    g7: LineSegment StartX=19.025 StartY=8.793 StartZ=0 EndX=19.025 EndY=18.793 EndZ=0
    g8: LineSegment StartX=19.025 StartY=18.793 StartZ=0 EndX=17.3886 EndY=18.793 EndZ=0
    g9: LineSegment StartX=17.3886 StartY=18.793 StartZ=0 EndX=17.3886 EndY=25.1014 EndZ=0
    g10: LineSegment StartX=6.375 StartY=18.793 StartZ=0 EndX=8.04245 EndY=18.793 EndZ=0
    g11: LineSegment StartX=8.04245 StartY=18.793 StartZ=0 EndX=8.04245 EndY=25.1014 EndZ=0
    g12: LineSegment StartX=6.375 StartY=8.793 StartZ=0 EndX=8.26567 EndY=8.793 EndZ=0
    g13: LineSegment StartX=8.26567 StartY=8.793 StartZ=0 EndX=8.26567 EndY=4.26908 EndZ=0
  constraints (30):
    c: Horizontal(g0)
    c: Horizontal(g1)
    c: Coincident(g1,g2)
    c: Vertical(g2)
    c: Coincident(g2,g3)
    c: Horizontal(g3)
    c: Horizontal(g4)
    c: Coincident(g4,g5)
    c: Vertical(g5)
    c: Coincident(g5,g6)
    c: Horizontal(g6)
    c: Coincident(g6,g7)
    c: Coincident(g7,g8)
    c: Horizontal(g8)
    c: Coincident(g8,g9)
    c: Coincident(g9,g0)
    c: Vertical(g9)
    c: Coincident(g7,g-8)
    c: Coincident(g6,g-9)
    c: Coincident(g3,g-10)
    c: Coincident(g1,g10)
    c: Horizontal(g10)
    c: Coincident(g10,g11)
    c: Coincident(g11,g0)
    c: Vertical(g11)
    c: Coincident(g3,g12)
    c: Horizontal(g12)
    c: Coincident(g12,g13)
    c: Coincident(g13,g4)
    c: Vertical(g13)
FEATURE [PartDesign::Pad] Pad001
  Direction = (0,0,1)
  Length = 9.3
  Length2 = 10
  Profile = -> Sketch013
  ReferenceAxis = -> Sketch013 [N_Axis]
  Refine = true
  Suppressed = false
  Type = 0
FEATURE [PartDesign::Pad] Pad002
  BaseFeature = -> Pad001
  Direction = (0,0,1)
  Length = 2
  Length2 = 10
  Profile = -> Sketch012
  ReferenceAxis = -> Sketch012 [N_Axis]
  Refine = true
  Reversed = true
  Suppressed = false
  Type = 0
FEATURE [PartDesign::Body] Body001  label="Body"
  AllowCompound = false
  Group = -> [ShapeBinder004,Sketch012,Sketch013,Pad001,Pad002]
  Origin = -> Origin012
  Tip = -> Pad002
FEATURE [Sketcher::SketchObject] Sketch014  label="2.4"
  ArcFitTolerance = 1e-06
  FullyConstrained = false
  MakeInternals = false
  sketch-geometry (8):
    g0: LineSegment StartX=-2.4 StartY=31.75 StartZ=0 EndX=-2.4 EndY=0 EndZ=0
    g1: ArcOfCircle CenterX=0 CenterY=0 CenterZ=0 NormalX=0 NormalY=0 NormalZ=1 AngleXU=0 Radius=2.4 StartAngle=3.14159 EndAngle=4.71239
    g2: LineSegment StartX=-4e-16 StartY=-2.4 StartZ=0 EndX=25.4 EndY=-2.4 EndZ=0
    g3: ArcOfCircle CenterX=25.4 CenterY=0 CenterZ=0 NormalX=0 NormalY=0 NormalZ=1 AngleXU=1.5708 Radius=2.4 StartAngle=3.14159 EndAngle=4.71239
    g4: LineSegment StartX=27.8 StartY=-4e-16 StartZ=0 EndX=27.8 EndY=31.75 EndZ=0
    g5: ArcOfCircle CenterX=25.4 CenterY=31.75 CenterZ=0 NormalX=0 NormalY=0 NormalZ=1 AngleXU=-3.14159 Radius=2.4 StartAngle=3.14159 EndAngle=4.71239
    g6: LineSegment StartX=25.4 StartY=34.15 StartZ=0 EndX=0 EndY=34.15 EndZ=0
    g7: ArcOfCircle CenterX=0 CenterY=31.75 CenterZ=0 NormalX=0 NormalY=0 NormalZ=1 AngleXU=-1.5708 Radius=2.4 StartAngle=3.14159 EndAngle=4.71239
  constraints (12):
    c: Vertical(g0)
    c: Coincident(g0,g1)
    c: Coincident(g1,g2)
    c: Horizontal(g2)
    c: Coincident(g2,g3)
    c: Coincident(g3,g4)
    c: Vertical(g4)
    c: Coincident(g4,g5)
    c: Coincident(g5,g6)
    c: Horizontal(g6)
    c: Coincident(g6,g7)
    c: Coincident(g7,g0)
FEATURE [PartDesign::ShapeBinder] ShapeBinder005
  Support = -> [Pcb_bbd4]
  TraceSupport = false
FEATURE [Sketcher::SketchObject] Sketch
  ArcFitTolerance = 1e-06
  AttachmentSupport = -> [XY_Plane013]
  ExternalGeometry = -> [ShapeBinder005]
  FullyConstrained = true
  MakeInternals = false
  MapMode = 5
  sketch-geometry (2):
    g0: LineSegment [constr] StartX=6.375 StartY=18.793 StartZ=0 EndX=19.025 EndY=8.793 EndZ=0
    g1: Circle CenterX=12.7 CenterY=13.793 CenterZ=0 NormalX=0 NormalY=0 NormalZ=1 AngleXU=0 Radius=2
  constraints (4):
    c: Coincident(g0,g-3)
    c: Coincident(g0,g-5)
    c: Symmetric(g0,g0,g1)
    c: Diameter(g1) = 4
FEATURE [PartDesign::Pad] Pad003
  Direction = (0,0,1)
  Length = 12
  Length2 = 10
  Profile = -> Sketch
  ReferenceAxis = -> Sketch [N_Axis]
  Refine = true
  Suppressed = false
  Type = 0
FEATURE [PartDesign::Body] Body002  label="stick"
  AllowCompound = false
  Group = -> [ShapeBinder005,Sketch,Pad003]
  Origin = -> Origin013
  Placement = pos=(0,0,6.5) rot=(0,0,1;0rad)
  Tip = -> Pad003
FEATURE [Part::Feature] Part__Feature001  label="Thumbstick"
  Placement = pos=(12.7,13.8,-2.8) rot=(0,0,1;0rad)
  shape: bbox 24.74 x 24.74 x 17.5 mm, 20 faces (baked)
FEATURE [App::Part] Part  label="thumbstick"
  Group = -> [Body001,Body002,Part__Feature001]
  Origin = -> Origin011
FEATURE [Sketcher::SketchObject] Sketch015  label="2.006"
  ArcFitTolerance = 1e-06
  FullyConstrained = false
  MakeInternals = false
  sketch-geometry (8):
    g0: LineSegment StartX=-2.4 StartY=31.75 StartZ=0 EndX=-2.4 EndY=0 EndZ=0
    g1: ArcOfCircle CenterX=0 CenterY=0 CenterZ=0 NormalX=0 NormalY=0 NormalZ=1 AngleXU=0 Radius=2.4 StartAngle=3.14159 EndAngle=4.71239
    g2: LineSegment StartX=-4e-16 StartY=-2.4 StartZ=0 EndX=25.4 EndY=-2.4 EndZ=0
    g3: ArcOfCircle CenterX=25.4 CenterY=0 CenterZ=0 NormalX=0 NormalY=0 NormalZ=1 AngleXU=1.5708 Radius=2.4 StartAngle=3.14159 EndAngle=4.71239
    g4: LineSegment StartX=27.8 StartY=-7e-16 StartZ=0 EndX=27.8 EndY=31.75 EndZ=0
    g5: ArcOfCircle CenterX=25.4 CenterY=31.75 CenterZ=0 NormalX=0 NormalY=0 NormalZ=1 AngleXU=-3.14159 Radius=2.4 StartAngle=3.14159 EndAngle=4.71239
    g6: LineSegment StartX=25.4 StartY=34.15 StartZ=0 EndX=0 EndY=34.15 EndZ=0
    g7: ArcOfCircle CenterX=0 CenterY=31.75 CenterZ=0 NormalX=0 NormalY=0 NormalZ=1 AngleXU=-1.5708 Radius=2.4 StartAngle=3.14159 EndAngle=4.71239
  constraints (12):
    c: Vertical(g0)
    c: Coincident(g0,g1)
    c: Coincident(g1,g2)
    c: Horizontal(g2)
    c: Coincident(g2,g3)
    c: Coincident(g3,g4)
    c: Vertical(g4)
    c: Coincident(g4,g5)
    c: Coincident(g5,g6)
    c: Horizontal(g6)
    c: Coincident(g6,g7)
    c: Coincident(g7,g0)
FEATURE [PartDesign::Pad] Pad004
  Direction = (0,0,1)
  Length = 5.3
  Length2 = 10
  Profile = -> Sketch015
  ReferenceAxis = -> Sketch015 [N_Axis]
  Refine = true
  Suppressed = false
  Type = 0
FEATURE [PartDesign::Thickness] Thickness
  Base = -> Pad004 [Face9]
  BaseFeature = -> Pad004
  Intersection = false
  Join = 0
  Mode = 0
  Refine = true
  Reversed = true
  SupportTransform = false
  Suppressed = false
  Value = 2
FEATURE [PartDesign::ShapeBinder] ShapeBinder006
  Support = -> [Pocket003]
  TraceSupport = false
FEATURE [Sketcher::SketchObject] Sketch016
  ArcFitTolerance = 1e-06
  AttachmentSupport = -> [Thickness]
  ExternalGeometry = -> [ShapeBinder006]
  FullyConstrained = true
  MakeInternals = false
  MapMode = 5
  Placement = pos=(0,0,0) rot=(1,0,0;3.14159rad)
  sketch-geometry (8):
    g0: Circle CenterX=2.54 CenterY=-2.54 CenterZ=0 NormalX=0 NormalY=0 NormalZ=1 AngleXU=0 Radius=3
    g1: Circle CenterX=22.86 CenterY=-2.54 CenterZ=0 NormalX=0 NormalY=0 NormalZ=1 AngleXU=0 Radius=3
    g2: Circle CenterX=22.86 CenterY=-29.21 CenterZ=0 NormalX=0 NormalY=0 NormalZ=1 AngleXU=0 Radius=3
    g3: Circle CenterX=2.54 CenterY=-29.21 CenterZ=0 NormalX=0 NormalY=0 NormalZ=1 AngleXU=0 Radius=3
    g4: Circle CenterX=2.54 CenterY=-2.54 CenterZ=0 NormalX=0 NormalY=0 NormalZ=1 AngleXU=0 Radius=1.65
    g5: Circle CenterX=22.86 CenterY=-2.54 CenterZ=0 NormalX=0 NormalY=0 NormalZ=1 AngleXU=0 Radius=1.65
    g6: Circle CenterX=22.86 CenterY=-29.21 CenterZ=0 NormalX=0 NormalY=0 NormalZ=1 AngleXU=0 Radius=1.65
    g7: Circle CenterX=2.54 CenterY=-29.21 CenterZ=0 NormalX=0 NormalY=0 NormalZ=1 AngleXU=0 Radius=1.65
  constraints (16):
    c: Diameter(g0) = 6
    c: Coincident(g0,g-3)
    c: Diameter(g1) = 6
    c: Coincident(g1,g-4)
    c: Diameter(g2) = 6
    c: Coincident(g2,g-5)
    c: Diameter(g3) = 6
    c: Coincident(g3,g-6)
    c: Diameter(g4) = 3.3
    c: Coincident(g4,g0)
    c: Diameter(g5) = 3.3
    c: Coincident(g5,g1)
    c: Diameter(g6) = 3.3
    c: Coincident(g6,g2)
    c: Diameter(g7) = 3.3
    c: Coincident(g7,g3)
FEATURE [Part::Ellipsoid] Ellipsoid
  Angle1 = -90
  Angle2 = 90
  Angle3 = 180
  AttacherType = Attacher::AttachEngine3D
  Placement = pos=(12.7,13.8,9.3) rot=(1,0,0;1.5708rad)
  Radius1 = 12.37
  Radius2 = 12.37
  Radius3 = 8
FEATURE [PartDesign::Plane] DatumPlane
  AttachmentOffset = pos=(0,0,12.7) rot=(0,0,1;0rad)
  AttachmentSupport = -> [YZ_Plane014]
  Length = 70.0266
  MapMode = 5
  Placement = pos=(12.7,0,0) rot=(0.57735,0.57735,0.57735;2.0944rad)
  ResizeMode = 0
  Width = 60.8766
FEATURE [Sketcher::SketchObject] Sketch017
  ArcFitTolerance = 1e-06
  AttachmentSupport = -> [DatumPlane]
  FullyConstrained = false
  MakeInternals = false
  MapMode = 5
  Placement = pos=(12.7,0,0) rot=(0.57735,0.57735,0.57735;2.0944rad)
  sketch-geometry (18):
    g0: Circle [constr] CenterX=29.1118 CenterY=3.8 CenterZ=0 NormalX=0 NormalY=0 NormalZ=1 AngleXU=0 Radius=1
    g1: Circle [constr] CenterX=30.0485 CenterY=13.7535 CenterZ=0 NormalX=0 NormalY=0 NormalZ=1 AngleXU=0 Radius=1
    g2: Circle [constr] CenterX=23.3909 CenterY=17.1877 CenterZ=0 NormalX=0 NormalY=0 NormalZ=1 AngleXU=0 Radius=1
    g3: BSplineCurve PolesCount=3 KnotsCount=2 Degree=2 IsPeriodic=0
    g4: GeomPoint [constr] X=29.1118 Y=3.8 Z=0
    g5: GeomPoint [constr] X=23.3909 Y=17.1877 Z=0
    g6: LineSegment StartX=23.3909 StartY=17.1877 StartZ=0 EndX=13.7824 EndY=17.1877 EndZ=0
    g7: Circle [constr] CenterX=28.1118 CenterY=3.8 CenterZ=0 NormalX=0 NormalY=0 NormalZ=1 AngleXU=0 Radius=1
    g8: Circle [constr] CenterX=28.4002 CenterY=12.6207 CenterZ=0 NormalX=0 NormalY=0 NormalZ=1 AngleXU=0 Radius=1
    g9: Circle [constr] CenterX=23.1917 CenterY=16.2077 CenterZ=0 NormalX=0 NormalY=0 NormalZ=1 AngleXU=0 Radius=1
    g10: BSplineCurve PolesCount=3 KnotsCount=2 Degree=2 IsPeriodic=0
    g11: GeomPoint [constr] X=28.1118 Y=3.8 Z=0
    g12: GeomPoint [constr] X=23.1917 Y=16.2077 Z=0
    g13: LineSegment StartX=28.1118 StartY=3.8 StartZ=0 EndX=29.1118 EndY=3.8 EndZ=0
    g14: LineSegment StartX=13.7824 StartY=17.1877 StartZ=0 EndX=13.7824 EndY=16.2077 EndZ=0
    g15: LineSegment StartX=13.7824 StartY=16.2077 StartZ=0 EndX=23.1917 EndY=16.2077 EndZ=0
    g16: LineSegment [constr] StartX=1.40969 StartY=9.23031 StartZ=0 EndX=26.155 EndY=9.23031 EndZ=0
    g17: LineSegment [constr] StartX=13.7824 StartY=9.23031 StartZ=0 EndX=13.7824 EndY=17.9973 EndZ=0
  constraints (33):
    c: Weight(g0) = 1
    c: Equal(g0,g1)
    c: Equal(g0,g2)
    c: InternalAlignment(g0,g3)
    c: InternalAlignment(g1,g3)
    c: InternalAlignment(g2,g3)
    c: InternalAlignment(g4,g3)
    c: InternalAlignment(g5,g3)
    c: Coincident(g6,g3)
    c: Horizontal(g6)
    c: Weight(g7) = 1
    c: Equal(g7,g8)
    c: Equal(g7,g9)
    c: InternalAlignment(g7,g10)
    c: InternalAlignment(g8,g10)
    c: InternalAlignment(g9,g10)
    c: InternalAlignment(g11,g10)
    c: InternalAlignment(g12,g10)
    c: Coincident(g13,g10)
    c: Coincident(g13,g3)
    c: Horizontal(g13)
    c: DistanceX(g13,g13) = 1
    c: Distance(g3,g10) = 1
    c: Distance(g1,g8) = 2
    c: Coincident(g6,g14)
    c: Vertical(g14)
    c: Coincident(g15,g10)
    c: Horizontal(g15)
    c: Horizontal(g16)
    c: Symmetric(g16,g16,g17)
    c: Vertical(g17)
    c: PointOnObject(g6,g17)
    c: Distance(g10,g-3) = 1.5
FEATURE [PartDesign::Chamfer] Chamfer
  Angle = 45
  Base = -> Thickness [Edge4]
  BaseFeature = -> Thickness
  ChamferType = 0
  FlipDirection = false
  Refine = true
  Size = 1.5
  Size2 = 1
  SupportTransform = false
  Suppressed = false
  UseAllEdges = false
FEATURE [PartDesign::Pad] Pad005
  BaseFeature = -> Chamfer
  Direction = (0,0,-1)
  Length = 3.3
  Length2 = 10
  Profile = -> Sketch016
  ReferenceAxis = -> Sketch016 [N_Axis]
  Refine = true
  Reversed = true
  Suppressed = false
  Type = 0
FEATURE [PartDesign::Revolution] Revolution
  Angle = 360
  Angle2 = 60
  Axis = (0,0,-1)
  Base = (12.7,13.7824,17.1877)
  BaseFeature = -> Pad005
  Profile = -> Sketch017
  ReferenceAxis = -> Sketch017 [Edge4]
  Refine = true
  Reversed = true
  Suppressed = false
  Type = 0
FEATURE [Sketcher::SketchObject] Sketch018
  ArcFitTolerance = 1e-06
  AttachmentSupport = -> [Revolution]
  ExternalGeometry = -> [Revolution]
  FullyConstrained = true
  MakeInternals = false
  MapMode = 5
  Placement = pos=(0,0,17.1877) rot=(0,0,1;0rad)
  sketch-geometry (1):
    g0: Circle CenterX=12.7 CenterY=13.7824 CenterZ=0 NormalX=0 NormalY=0 NormalZ=1 AngleXU=0 Radius=9.5
  constraints (2):
    c: Coincident(g0,g-3)
    c: Diameter(g0) = 19
FEATURE [PartDesign::Pocket] Pocket
  BaseFeature = -> Revolution
  Direction = (0,0,-1)
  Length = 14
  Length2 = 5
  Profile = -> Sketch018
  ReferenceAxis = -> Sketch018 [N_Axis]
  Refine = true
  Suppressed = false
  Type = 0
FEATURE [Sketcher::SketchObject] Sketch019
  ArcFitTolerance = 1e-06
  AttachmentSupport = -> [Pocket]
  FullyConstrained = true
  MakeInternals = false
  MapMode = 5
  Placement = pos=(0,0,5.3) rot=(0,0,1;0rad)
  sketch-geometry (1):
    g0: Circle CenterX=12.7 CenterY=13.7824 CenterZ=0 NormalX=0 NormalY=0 NormalZ=1 AngleXU=0 Radius=14.157
  constraints (2):
    c: Coincident(g0,g-3)
    c: Equal(g0,g-3)
FEATURE [PartDesign::Pocket] Pocket004
  BaseFeature = -> Pocket
  Direction = (0,0,-1)
  Length = 2
  Length2 = 5
  Profile = -> Sketch019
  ReferenceAxis = -> Sketch019 [N_Axis]
  Refine = true
  Suppressed = false
  Type = 0
FEATURE [Sketcher::SketchObject] Sketch020
  ArcFitTolerance = 1e-06
  AttachmentSupport = -> [Pocket004]
  ExternalGeometry = -> [Pocket004]
  FullyConstrained = false
  MakeInternals = false
  MapMode = 5
  Placement = pos=(0,34.15,0) rot=(0,0.707107,0.707107;3.14159rad)
  sketch-geometry (4):
    g0: LineSegment StartX=-15.1629 StartY=0 StartZ=0 EndX=-10.1629 EndY=0 EndZ=0
    g1: LineSegment StartX=-10.1629 StartY=0 StartZ=0 EndX=-10.1629 EndY=1.3 EndZ=0
    g2: LineSegment StartX=-10.1629 StartY=1.3 StartZ=0 EndX=-15.1629 EndY=1.3 EndZ=0
    g3: LineSegment StartX=-15.1629 StartY=1.3 StartZ=0 EndX=-15.1629 EndY=0 EndZ=0
  constraints (11):
    c: Coincident(g0,g1)
    c: Coincident(g1,g2)
    c: Coincident(g2,g3)
    c: Coincident(g3,g0)
    c: Horizontal(g0)
    c: Horizontal(g2)
    c: Vertical(g1)
    c: Vertical(g3)
    c: PointOnObject(g0,g-3)
    c: DistanceX(g2,g2) = 5
    c: DistanceY(g1,g1) = 1.3
FEATURE [PartDesign::Pocket] Pocket005
  BaseFeature = -> Pocket004
  Direction = (0,-1,2e-16)
  Length = 2
  Length2 = 5
  Profile = -> Sketch020
  ReferenceAxis = -> Sketch020 [N_Axis]
  Refine = true
  Suppressed = false
  Type = 0
FEATURE [PartDesign::Body] Body003  label="top"
  AllowCompound = false
  Group = -> [Sketch015,Pad004,Thickness,Chamfer,ShapeBinder006,Sketch016,Pad005,DatumPlane,Sketch017,Revolution,Sketch018,Pocket,Sketch019,Pocket004,Sketch020,Pocket005]
  Origin = -> Origin014
  Tip = -> Pocket005
FEATURE [App::Part] Part001  label="case"
  Group = -> [Body,Body003,Ellipsoid]
  Origin = -> Origin009
---- part trackball-holder.FCStd = doc fcstd_ebb0a6e7c5ac ----
FCSTD DOCUMENT  (FreeCAD 1.0RUnknown)
Label: trackball-holder
License: All rights reserved
LicenseURL: https://en.wikipedia.org/wiki/All_rights_reserved
objects: Part::Feature×37, Sketcher::SketchObject×18, PartDesign::Pocket×13, App::Part×5, PartDesign::Pad×5, PartDesign::Body×3, PartDesign::FeatureBase×2, PartDesign::Chamfer×2, PartDesign::Fillet×1, PartDesign::SubShapeBinder×1
note: 144 computed .brp shape members not serialized (recipe doc carries the construction recipe); baked Part::Feature solids carry a one-line shape summary decoded from their .brp

FEATURE [Part::Feature] Part__Feature  label="Trackball"
  Placement = pos=(29,32,-7.8) rot=(0,0,1;0rad)
  shape: bbox 34 x 34 x 34 mm, 1 faces (baked)
FEATURE [Part::Feature] Part__Feature001  label="Static bearing"
  Placement = pos=(29,32,-7.8) rot=(0,0,1;0rad)
  shape: bbox 3 x 3 x 3 mm, 1 faces (baked)
FEATURE [Part::Feature] Part__Feature003  label="Static bearing001"
  Placement = pos=(29,32,-7.8) rot=(0,0,1;0rad)
  shape: bbox 3 x 3 x 3 mm, 1 faces (baked)
FEATURE [Part::Feature] Part__Feature004  label="Bearing holder"
  Placement = pos=(29,32,-7.8) rot=(0,0,1;0rad)
  shape: bbox 9.742 x 7.809 x 9.716 mm, 12 faces (baked)
FEATURE [Part::Feature] Part__Feature006  label="Static bearing002"
  Placement = pos=(29,32,-7.8) rot=(0,0,1;0rad)
  shape: bbox 3 x 3 x 3 mm, 1 faces (baked)
FEATURE [Part::Feature] Part__Feature007  label="Bearing holder001"
  Placement = pos=(29,32,-7.8) rot=(0,0,1;0rad)
  shape: bbox 8.97 x 9.681 x 9.716 mm, 12 faces (baked)
FEATURE [Part::Feature] Part__Feature008  label="Trackball-holder"
  Placement = pos=(29,32,-7.8) rot=(0,0,1;0rad)
  shape: bbox 43.85 x 39.78 x 21.7 mm, 196 faces (baked)
FEATURE [Part::Feature] Part__Feature009  label="Bearing holder002"
  Placement = pos=(29,32,-7.8) rot=(0,0,1;0rad)
  shape: bbox 8.97 x 9.681 x 9.716 mm, 12 faces (baked)
FEATURE [Part::Feature] Part__Feature010  label="Lead"
  shape: bbox 0.9 x 0.5 x 4.51 mm, 14 faces (baked)
FEATURE [Part::Feature] Part__Feature011  label="Lead001"
  Placement = pos=(-7.11e-14,-1.78,0) rot=(0,0,1;0rad)
  shape: bbox 0.9 x 0.5 x 4.51 mm, 14 faces (baked)
FEATURE [Part::Feature] Part__Feature012  label="Lead002"
  Placement = pos=(-1.78e-14,-3.56,0) rot=(0,0,1;0rad)
  shape: bbox 0.9 x 0.5 x 4.51 mm, 14 faces (baked)
FEATURE [Part::Feature] Part__Feature013  label="Lead003"
  Placement = pos=(-1.066e-13,-5.34,0) rot=(0,0,1;0rad)
  shape: bbox 0.9 x 0.5 x 4.51 mm, 14 faces (baked)
FEATURE [Part::Feature] Part__Feature014  label="Lead004"
  Placement = pos=(-7.11e-14,-7.12,0) rot=(0,0,1;0rad)
  shape: bbox 0.9 x 0.5 x 4.51 mm, 14 faces (baked)
FEATURE [Part::Feature] Part__Feature015  label="Lead005"
  Placement = pos=(-1.243e-13,-8.9,6e-16) rot=(0,0,1;0rad)
  shape: bbox 0.9 x 0.5 x 4.51 mm, 14 faces (baked)
FEATURE [Part::Feature] Part__Feature016  label="Lead006"
  Placement = pos=(-7.11e-14,-10.68,-6e-16) rot=(0,0,1;0rad)
  shape: bbox 0.9 x 0.5 x 4.51 mm, 14 faces (baked)
FEATURE [Part::Feature] Part__Feature017  label="Lead007"
  Placement = pos=(-7.11e-14,-12.46,-6e-16) rot=(0,0,1;0rad)
  shape: bbox 0.9 x 0.5 x 4.51 mm, 14 faces (baked)
FEATURE [Part::Feature] Part__Feature018  label="Lead(Mirror)"
  Placement = pos=(-1.78e-14,-0.89,0) rot=(0,1,0;3.14159rad)
  shape: bbox 0.9 x 0.5 x 4.51 mm, 14 faces (baked)
FEATURE [Part::Feature] Part__Feature019  label="Lead(Mirror)001"
  Placement = pos=(-1.78e-14,-2.67,0) rot=(0,1,0;3.14159rad)
  shape: bbox 0.9 x 0.5 x 4.51 mm, 14 faces (baked)
FEATURE [Part::Feature] Part__Feature020  label="Lead(Mirror)002"
  Placement = pos=(3.55e-14,-4.45,0) rot=(0,1,0;3.14159rad)
  shape: bbox 0.9 x 0.5 x 4.51 mm, 14 faces (baked)
FEATURE [Part::Feature] Part__Feature021  label="Lead(Mirror)003"
  Placement = pos=(1.78e-14,-6.23,0) rot=(0,1,0;3.14159rad)
  shape: bbox 0.9 x 0.5 x 4.51 mm, 14 faces (baked)
FEATURE [Part::Feature] Part__Feature022  label="Lead(Mirror)004"
  Placement = pos=(-3.55e-14,-8.01,6e-16) rot=(0,1,0;3.14159rad)
  shape: bbox 0.9 x 0.5 x 4.51 mm, 14 faces (baked)
FEATURE [Part::Feature] Part__Feature023  label="Lead(Mirror)005"
  Placement = pos=(1.78e-14,-9.79,6e-16) rot=(0,1,0;3.14159rad)
  shape: bbox 0.9 x 0.5 x 4.51 mm, 14 faces (baked)
FEATURE [Part::Feature] Part__Feature024  label="Lead(Mirror)006"
  Placement = pos=(-3.55e-14,-11.57,-6e-16) rot=(0,1,0;3.14159rad)
  shape: bbox 0.9 x 0.5 x 4.51 mm, 14 faces (baked)
FEATURE [Part::Feature] Part__Feature025  label="Lead(Mirror)007"
  Placement = pos=(-3.55e-14,-13.35,-6e-16) rot=(0,1,0;3.14159rad)
  shape: bbox 0.9 x 0.5 x 4.51 mm, 14 faces (baked)
FEATURE [Part::Feature] Part__Feature026  label="SOLID"
  shape: bbox 10.1 x 16.2 x 2.21 mm, 48 faces (baked)
FEATURE [App::Part] Chip
  Group = -> [Part__Feature010,Part__Feature011,Part__Feature012,Part__Feature013,Part__Feature014,Part__Feature015,Part__Feature016,Part__Feature017,Part__Feature018,Part__Feature019,Part__Feature020,Part__Feature021,Part__Feature022,Part__Feature023,Part__Feature024,Part__Feature025,Part__Feature026]
  Origin = -> Origin001
  Placement = pos=(0,0,1e-16) rot=(0,0,1;0rad)
FEATURE [Part::Feature] Part__Feature027  label="Lens"
  Placement = pos=(0,0,-6.27) rot=(0,0,1;0rad)
  shape: bbox 18.86 x 21.16 x 8.475 mm, 85 faces (baked)
FEATURE [Part::Feature] Part__Feature028  label="PMW3360DM PCB"
  Placement = pos=(-104.986,-148.495,-3.79) rot=(0,0,1;1.5708rad)
  shape: bbox 21 x 28 x 1.58 mm, 36 faces (baked)
FEATURE [App::Part] PMW3360_v12_v1  label="PMW3360 v12 v1"
  Group = -> [Chip,Part__Feature027,Part__Feature028]
  Origin = -> Origin002
  Placement = pos=(0,0,-4) rot=(-0.707107,0.707107,0;3.14159rad)
FEATURE [Part::Feature] Part__Feature029  label="FusionComponent"
  Placement = pos=(148.5,105,0) rot=(0,1,0;3.14159rad)
  shape: bbox 38.01 x 31.01 x 5.805 mm, 57 faces (baked)
FEATURE [PartDesign::FeatureBase] BaseFeature
  BaseFeature = -> Part__Feature008
  Suppressed = false
FEATURE [Sketcher::SketchObject] Sketch
  ArcFitTolerance = 1e-06
  AttachmentSupport = -> [BaseFeature]
  ExternalGeometry = -> [BaseFeature]
  FullyConstrained = true
  MakeInternals = false
  MapMode = 5
  Placement = pos=(-5e-16,1.2e-15,7.79) rot=(1,0,0;3.14159rad)
  sketch-geometry (2):
    g0: Circle CenterX=-43.692 CenterY=31.5043 CenterZ=0 NormalX=0 NormalY=0 NormalZ=1 AngleXU=0 Radius=2.2
    g1: Circle CenterX=-14.692 CenterY=31.5043 CenterZ=0 NormalX=0 NormalY=0 NormalZ=1 AngleXU=0 Radius=2.2
  constraints (4):
    c: Coincident(g0,g-3)
    c: Equal(g0,g-3)
    c: Coincident(g1,g-4)
    c: Equal(g1,g-4)
FEATURE [PartDesign::Pad] Pad
  BaseFeature = -> BaseFeature
  Direction = (0,0,-1)
  Length = 7
  Length2 = 10
  Profile = -> Sketch
  ReferenceAxis = -> Sketch [N_Axis]
  Refine = true
  Reversed = true
  Suppressed = false
  Type = 0
FEATURE [Sketcher::SketchObject] Sketch001
  ArcFitTolerance = 1e-06
  AttachmentSupport = -> [Pad]
  ExternalGeometry = -> [Pad]
  FullyConstrained = true
  MakeInternals = false
  MapMode = 5
  Placement = pos=(-38.692,-1.24e-14,0) rot=(0.57735,0.57735,0.57735;2.0944rad)
  sketch-geometry (4):
    g0: LineSegment StartX=-42.2543 StartY=11.29 StartZ=0 EndX=-42.2543 EndY=7.79 EndZ=0
    g1: LineSegment StartX=-42.2543 StartY=7.79 StartZ=0 EndX=-20.7543 EndY=7.79 EndZ=0
    g2: LineSegment StartX=-20.7543 StartY=7.79 StartZ=0 EndX=-20.7543 EndY=11.29 EndZ=0
    g3: LineSegment StartX=-20.7543 StartY=11.29 StartZ=0 EndX=-42.2543 EndY=11.29 EndZ=0
  constraints (10):
    c: Coincident(g0,g1)
    c: Coincident(g1,g2)
    c: Coincident(g2,g3)
    c: Coincident(g3,g0)
    c: Vertical(g0)
    c: Vertical(g2)
    c: Horizontal(g1)
    c: Horizontal(g3)
    c: Coincident(g0,g-4)
    c: Coincident(g1,g-6)
FEATURE [Sketcher::SketchObject] Sketch004
  ArcFitTolerance = 1e-06
  AttachmentSupport = -> [XY_Plane005]
  FullyConstrained = false
  MakeInternals = false
  MapMode = 5
  sketch-geometry (12):
    g0: LineSegment StartX=20.4375 StartY=-12.0318 StartZ=0 EndX=20.4375 EndY=13.6286 EndZ=0
    g1: LineSegment StartX=16.2108 StartY=17.8553 StartZ=0 EndX=-16.5296 EndY=17.8553 EndZ=0
    g2: LineSegment StartX=-21.4525 StartY=12.9324 StartZ=0 EndX=-21.4525 EndY=-12.728 EndZ=0
    g3: LineSegment StartX=-17.2258 StartY=-16.9547 StartZ=0 EndX=15.5146 EndY=-16.9547 EndZ=0
    g4: ArcOfCircle CenterX=-16.5296 CenterY=12.9324 CenterZ=0 NormalX=0 NormalY=0 NormalZ=1 AngleXU=0 Radius=4.92288 StartAngle=1.5708 EndAngle=3.14159
    g5: GeomPoint [constr] X=-21.4525 Y=17.8553 Z=0
    g6: ArcOfCircle CenterX=-17.2258 CenterY=-12.728 CenterZ=0 NormalX=0 NormalY=0 NormalZ=1 AngleXU=0 Radius=4.22668 StartAngle=3.14159 EndAngle=4.71239
    g7: GeomPoint [constr] X=-21.4525 Y=-16.9547 Z=0
    g8: ArcOfCircle CenterX=15.5146 CenterY=-12.0318 CenterZ=0 NormalX=0 NormalY=0 NormalZ=1 AngleXU=0 Radius=4.92288 StartAngle=4.71239 EndAngle=6.28319
    g9: GeomPoint [constr] X=20.4375 Y=-16.9547 Z=0
    g10: ArcOfCircle CenterX=16.2108 CenterY=13.6286 CenterZ=0 NormalX=0 NormalY=0 NormalZ=1 AngleXU=0 Radius=4.22668 StartAngle=0 EndAngle=1.5708
    g11: GeomPoint [constr] X=20.4375 Y=17.8553 Z=0
  constraints (22):
    c: Vertical(g0)
    c: Vertical(g2)
    c: Horizontal(g1)
    c: Horizontal(g3)
    c: DistanceX(g5,g11) = 41.89
    c: DistanceY(g9,g11) = 34.81
    c: PointOnObject(g5,g1)
    c: PointOnObject(g5,g2)
    c: Tangent(g1,g4) = -1.5708
    c: Tangent(g2,g4) = -1.5708
    c: PointOnObject(g7,g2)
    c: PointOnObject(g7,g3)
    c: Tangent(g2,g6) = -1.5708
    c: Tangent(g3,g6) = -1.5708
    c: PointOnObject(g9,g0)
    c: PointOnObject(g9,g3)
    c: Tangent(g0,g8) = -1.5708
    c: Tangent(g3,g8) = -1.5708
    c: PointOnObject(g11,g0)
    c: PointOnObject(g11,g1)
    c: Tangent(g0,g10) = -1.5708
    c: Tangent(g1,g10) = -1.5708
FEATURE [PartDesign::Pad] Pad001
  Direction = (0,0,1)
  Length = 7
  Length2 = 10
  Profile = -> Sketch004
  ReferenceAxis = -> Sketch004 [N_Axis]
  Refine = true
  Reversed = true
  Suppressed = false
  Type = 0
FEATURE [Sketcher::SketchObject] Sketch005
  ArcFitTolerance = 1e-06
  AttachmentSupport = -> [Pad001]
  FullyConstrained = false
  MakeInternals = false
  MapMode = 5
  sketch-geometry (4):
    g0: LineSegment StartX=-14.2525 StartY=10.6553 StartZ=0 EndX=-14.2525 EndY=-10.7575 EndZ=0
    g1: LineSegment StartX=-14.2525 StartY=-10.7575 StartZ=0 EndX=14.2358 EndY=-10.7575 EndZ=0
    g2: LineSegment StartX=14.2358 StartY=-10.7575 StartZ=0 EndX=14.2358 EndY=10.6553 EndZ=0
    g3: LineSegment StartX=14.2358 StartY=10.6553 StartZ=0 EndX=-14.2525 EndY=10.6553 EndZ=0
  constraints (8):
    c: Coincident(g0,g1)
    c: Coincident(g1,g2)
    c: Coincident(g2,g3)
    c: Coincident(g3,g0)
    c: Vertical(g0)
    c: Vertical(g2)
    c: Horizontal(g1)
    c: Horizontal(g3)
FEATURE [PartDesign::Pocket] Pocket002
  BaseFeature = -> Pad001
  Direction = (0,0,-1)
  Length = 3
  Length2 = 5
  Profile = -> Sketch005
  ReferenceAxis = -> Sketch005 [N_Axis]
  Refine = true
  Suppressed = false
  Type = 0
FEATURE [Sketcher::SketchObject] Sketch006
  ArcFitTolerance = 1e-06
  AttachmentSupport = -> [Pocket002]
  FullyConstrained = false
  MakeInternals = false
  MapMode = 5
  Placement = pos=(0,0,-3) rot=(0,0,1;0rad)
  sketch-geometry (14):
    g0: LineSegment [constr] StartX=13.2232 StartY=1.19515 StartZ=0 EndX=10.7894 EndY=1.19515 EndZ=0
    g1: LineSegment [constr] StartX=10.7894 StartY=1.19515 StartZ=0 EndX=10.7894 EndY=-1.23867 EndZ=0
    g2: LineSegment [constr] StartX=10.7894 StartY=-1.23867 StartZ=0 EndX=13.2232 EndY=-1.23867 EndZ=0
    g3: LineSegment [constr] StartX=13.2232 StartY=-1.23867 StartZ=0 EndX=13.2232 EndY=1.19515 EndZ=0
    g4: LineSegment [constr] StartX=12.0063 StartY=1.19515 StartZ=0 EndX=12.0063 EndY=-1.23867 EndZ=0
    g5: GeomPoint X=12.0063 Y=-0.0217585 Z=0
    g6: Circle CenterX=12.0063 CenterY=-0.0217585 CenterZ=0 NormalX=0 NormalY=0 NormalZ=1 AngleXU=0 Radius=1.65
    g7: LineSegment [constr] StartX=-10.7512 StartY=1.20514 StartZ=0 EndX=-13.2417 EndY=1.20514 EndZ=0
    g8: LineSegment [constr] StartX=-13.2417 StartY=1.20514 StartZ=0 EndX=-13.2417 EndY=-1.23653 EndZ=0
    g9: LineSegment [constr] StartX=-13.2417 StartY=-1.23653 StartZ=0 EndX=-10.7512 EndY=-1.23653 EndZ=0
    g10: LineSegment [constr] StartX=-10.7512 StartY=-1.23653 StartZ=0 EndX=-10.7512 EndY=1.20514 EndZ=0
    g11: LineSegment [constr] StartX=-11.9964 StartY=1.20514 StartZ=0 EndX=-11.9964 EndY=-1.23653 EndZ=0
    g12: GeomPoint [constr] X=-11.9964 Y=-0.015697 Z=0
    g13: Circle CenterX=-11.9964 CenterY=-0.015697 CenterZ=0 NormalX=0 NormalY=0 NormalZ=1 AngleXU=0 Radius=1.65
  constraints (26):
    c: Coincident(g0,g1)
    c: Coincident(g1,g2)
    c: Coincident(g2,g3)
    c: Coincident(g3,g0)
    c: Horizontal(g0)
    c: Horizontal(g2)
    c: Vertical(g1)
    c: Vertical(g3)
    c: Symmetric(g0,g0,g4)
    c: Symmetric(g2,g2,g4)
    c: Symmetric(g4,g4,g5)
    c: Diameter(g6) = 3.3
    c: Coincident(g6,g5)
    c: Coincident(g7,g8)
    c: Coincident(g8,g9)
    c: Coincident(g9,g10)
    c: Coincident(g10,g7)
    c: Horizontal(g7)
    c: Horizontal(g9)
    c: Vertical(g8)
    c: Vertical(g10)
    c: Symmetric(g7,g7,g11)
    c: Symmetric(g9,g9,g11)
    c: Symmetric(g11,g11,g12)
    c: Diameter(g13) = 3.3
    c: Coincident(g13,g12)
FEATURE [PartDesign::Pocket] Pocket003
  BaseFeature = -> Pocket002
  Direction = (0,0,-1)
  Length = 3.3
  Length2 = 5
  Profile = -> Sketch006
  ReferenceAxis = -> Sketch006 [N_Axis]
  Refine = true
  Suppressed = false
  Type = 0
FEATURE [Sketcher::SketchObject] Sketch007
  ArcFitTolerance = 1e-06
  AttachmentSupport = -> [Pocket003]
  FullyConstrained = true
  MakeInternals = false
  MapMode = 5
  sketch-geometry (4):
    g0: Circle CenterX=-18.4525 CenterY=14.8553 CenterZ=0 NormalX=0 NormalY=0 NormalZ=1 AngleXU=0 Radius=1.25
    g1: Circle CenterX=17.4375 CenterY=14.8553 CenterZ=0 NormalX=0 NormalY=0 NormalZ=1 AngleXU=0 Radius=1.25
    g2: Circle CenterX=17.4375 CenterY=-13.9547 CenterZ=0 NormalX=0 NormalY=0 NormalZ=1 AngleXU=0 Radius=1.25
    g3: Circle CenterX=-18.4525 CenterY=-13.9547 CenterZ=0 NormalX=0 NormalY=0 NormalZ=1 AngleXU=0 Radius=1.25
  constraints (12):
    c: Diameter(g0) = 2.5
    c: Diameter(g1) = 2.5
    c: Diameter(g2) = 2.5
    c: Diameter(g3) = 2.5
    c: Distance(g0,g-3) = 3
    c: Distance(g0,g-4) = 3
    c: Distance(g1,g-6) = 3
    c: Distance(g1,g-3) = 3
    c: Distance(g2,g-6) = 3
    c: Distance(g2,g-5) = 3
    c: Distance(g3,g-5) = 3
    c: Distance(g3,g-4) = 3
FEATURE [Sketcher::SketchObject] Sketch008
  ArcFitTolerance = 1e-06
  AttachmentSupport = -> [Pocket003]
  ExternalGeometry = -> [Pocket003]
  FullyConstrained = true
  MakeInternals = false
  MapMode = 5
  Placement = pos=(0,0,-7) rot=(1,0,0;3.14159rad)
  sketch-geometry (8):
    g0: LineSegment StartX=15.2358 StartY=-11.6553 StartZ=0 EndX=15.2358 EndY=11.7575 EndZ=0
    g1: LineSegment StartX=15.2358 StartY=11.7575 StartZ=0 EndX=-15.2525 EndY=11.7575 EndZ=0
    g2: LineSegment StartX=-15.2525 StartY=11.7575 StartZ=0 EndX=-15.2525 EndY=-11.6553 EndZ=0
    g3: LineSegment StartX=-15.2525 StartY=-11.6553 StartZ=0 EndX=15.2358 EndY=-11.6553 EndZ=0
    g4: LineSegment StartX=-21.4525 StartY=16.9547 StartZ=0 EndX=-21.4525 EndY=-17.8553 EndZ=0
    g5: LineSegment StartX=-21.4525 StartY=-17.8553 StartZ=0 EndX=20.4375 EndY=-17.8553 EndZ=0
    g6: LineSegment StartX=20.4375 StartY=-17.8553 StartZ=0 EndX=20.4375 EndY=16.9547 EndZ=0
    g7: LineSegment StartX=20.4375 StartY=16.9547 StartZ=0 EndX=-21.4525 EndY=16.9547 EndZ=0
  constraints (22):
    c: Coincident(g0,g1)
    c: Coincident(g1,g2)
    c: Coincident(g2,g3)
    c: Coincident(g3,g0)
    c: Vertical(g0)
    c: Vertical(g2)
    c: Horizontal(g1)
    c: Horizontal(g3)
    c: Distance(g3,g-3) = 1
    c: Distance(g-4,g2) = 1
    c: Distance(g-6,g1) = 1
    c: Distance(g0,g-5) = 1
    c: Coincident(g4,g5)
    c: Coincident(g5,g6)
    c: Coincident(g6,g7)
    c: Coincident(g7,g4)
    c: Vertical(g4)
    c: Vertical(g6)
    c: Horizontal(g5)
    c: Horizontal(g7)
    c: Coincident(g4,g-8)
    c: Coincident(g5,g-10)
FEATURE [PartDesign::Pocket] Pocket004
  BaseFeature = -> Pocket003
  Direction = (0,0,-1)
  Length = 5
  Length2 = 5
  Profile = -> Sketch007
  ReferenceAxis = -> Sketch007 [N_Axis]
  Refine = true
  Suppressed = false
  Type = 1
FEATURE [Sketcher::SketchObject] Sketch009
  ArcFitTolerance = 1e-06
  FullyConstrained = false
  MakeInternals = false
  MapMode = 5
  Placement = pos=(0,0,-2) rot=(0,0,1;0rad)
  sketch-geometry (4):
    g0: LineSegment StartX=-8.69214 StartY=6.13703 StartZ=0 EndX=-8.69214 EndY=-6.47788 EndZ=0
    g1: LineSegment StartX=-8.69214 StartY=-6.47788 StartZ=0 EndX=9.36906 EndY=-6.47788 EndZ=0
    g2: LineSegment StartX=9.36906 StartY=-6.47788 StartZ=0 EndX=9.36906 EndY=6.13703 EndZ=0
    g3: LineSegment StartX=9.36906 StartY=6.13703 StartZ=0 EndX=-8.69214 EndY=6.13703 EndZ=0
  constraints (8):
    c: Coincident(g0,g1)
    c: Coincident(g1,g2)
    c: Coincident(g2,g3)
    c: Coincident(g3,g0)
    c: Vertical(g0)
    c: Vertical(g2)
    c: Horizontal(g1)
    c: Horizontal(g3)
FEATURE [PartDesign::Pocket] Pocket006
  BaseFeature = -> Pocket004
  Direction = (0,0,-1)
  Length = 4
  Length2 = 5
  Profile = -> Sketch009
  ReferenceAxis = -> Sketch009 [N_Axis]
  Refine = true
  Suppressed = false
  Type = 0
FEATURE [PartDesign::Pocket] Pocket007
  BaseFeature = -> Pocket006
  Direction = (0,0,1)
  Length = 4
  Length2 = 5
  Profile = -> Sketch008
  ReferenceAxis = -> Sketch008 [N_Axis]
  Refine = true
  Suppressed = false
  Type = 0
FEATURE [PartDesign::Chamfer] Chamfer
  Angle = 51
  Base = -> Pocket007 [Edge28,Edge29,Edge35,Edge34]
  BaseFeature = -> Pocket007
  ChamferType = 2
  FlipDirection = false
  Refine = true
  Size = 0.8
  Size2 = 1
  SupportTransform = false
  Suppressed = false
  UseAllEdges = false
FEATURE [Sketcher::SketchObject] Sketch010
  ArcFitTolerance = 1e-06
  AttachmentSupport = -> [Chamfer]
  FullyConstrained = false
  MakeInternals = false
  MapMode = 5
  sketch-geometry (4):
    g0: LineSegment StartX=-11.4553 StartY=18.9185 StartZ=0 EndX=-11.4553 EndY=7.09251 EndZ=0
    g1: LineSegment StartX=-11.4553 StartY=7.09251 StartZ=0 EndX=11.1733 EndY=7.09251 EndZ=0
    g2: LineSegment StartX=11.1733 StartY=7.09251 StartZ=0 EndX=11.1733 EndY=18.9185 EndZ=0
    g3: LineSegment StartX=11.1733 StartY=18.9185 StartZ=0 EndX=-11.4553 EndY=18.9185 EndZ=0
  constraints (8):
    c: Coincident(g0,g1)
    c: Coincident(g1,g2)
    c: Coincident(g2,g3)
    c: Coincident(g3,g0)
    c: Vertical(g0)
    c: Vertical(g2)
    c: Horizontal(g1)
    c: Horizontal(g3)
FEATURE [PartDesign::Pocket] Pocket008
  BaseFeature = -> Chamfer
  Direction = (0,0,-1)
  Length = 5
  Length2 = 5
  Profile = -> Sketch010
  ReferenceAxis = -> Sketch010 [N_Axis]
  Refine = true
  Suppressed = false
  Type = 1
FEATURE [PartDesign::Body] Body001  label="base"
  AllowCompound = false
  Group = -> [Sketch004,Pad001,Sketch005,Pocket002,Sketch006,Pocket003,Sketch007,Sketch008,Pocket004,Sketch009,Pocket006,Pocket007,Chamfer,Sketch010,Pocket008]
  Origin = -> Origin005
  Placement = pos=(0,0,-0.2) rot=(0,0,1;0rad)
  Tip = -> Pocket008
FEATURE [PartDesign::Pocket] Pocket
  BaseFeature = -> Pad
  Direction = (-1,0,0)
  Length = 2
  Length2 = 5
  Profile = -> Sketch001
  ReferenceAxis = -> Sketch001 [N_Axis]
  Refine = true
  Suppressed = false
  Type = 0
FEATURE [Sketcher::SketchObject] Sketch002
  ArcFitTolerance = 1e-06
  AttachmentSupport = -> [Pocket]
  ExternalGeometry = -> [Pocket]
  FullyConstrained = true
  MakeInternals = false
  MapMode = 5
  Placement = pos=(-40.692,0,0) rot=(0.57735,0.57735,0.57735;2.0944rad)
  sketch-geometry (4):
    g0: LineSegment StartX=-42.2543 StartY=11.29 StartZ=0 EndX=-42.2543 EndY=7.79 EndZ=0
    g1: LineSegment StartX=-42.2543 StartY=7.79 StartZ=0 EndX=-20.7543 EndY=7.79 EndZ=0
    g2: LineSegment StartX=-20.7543 StartY=7.79 StartZ=0 EndX=-20.7543 EndY=11.29 EndZ=0
    g3: LineSegment StartX=-20.7543 StartY=11.29 StartZ=0 EndX=-42.2543 EndY=11.29 EndZ=0
  constraints (10):
    c: Coincident(g0,g1)
    c: Coincident(g1,g2)
    c: Coincident(g2,g3)
    c: Coincident(g3,g0)
    c: Vertical(g0)
    c: Vertical(g2)
    c: Horizontal(g1)
    c: Horizontal(g3)
    c: Coincident(g0,g-3)
    c: Coincident(g1,g-4)
FEATURE [PartDesign::Pocket] Pocket001
  BaseFeature = -> Pocket
  Direction = (-1,0,0)
  Length = 23
  Length2 = 5
  Profile = -> Sketch002
  ReferenceAxis = -> Sketch002 [N_Axis]
  Refine = true
  Reversed = true
  Suppressed = false
  Type = 0
FEATURE [Sketcher::SketchObject] Sketch011
  ArcFitTolerance = 1e-06
  AttachmentSupport = -> [Pocket001]
  FullyConstrained = false
  MakeInternals = false
  MapMode = 5
  Placement = pos=(0,2e-16,7.79) rot=(1,0,0;3.14159rad)
  sketch-geometry (8):
    g0: Circle [constr] CenterX=-47.4493 CenterY=45.4463 CenterZ=0 NormalX=0 NormalY=0 NormalZ=1 AngleXU=0 Radius=1.25
    g1: Circle [constr] CenterX=-11.5558 CenterY=45.4556 CenterZ=0 NormalX=0 NormalY=0 NormalZ=1 AngleXU=0 Radius=1.25
    g2: Circle [constr] CenterX=-11.5625 CenterY=16.6378 CenterZ=0 NormalX=0 NormalY=0 NormalZ=1 AngleXU=0 Radius=1.25
    g3: Circle [constr] CenterX=-47.4641 CenterY=16.6426 CenterZ=0 NormalX=0 NormalY=0 NormalZ=1 AngleXU=0 Radius=1.25
    g4: Circle CenterX=-47.4493 CenterY=45.4463 CenterZ=0 NormalX=0 NormalY=0 NormalZ=1 AngleXU=0 Radius=1.65
    g5: Circle CenterX=-11.5558 CenterY=45.4556 CenterZ=0 NormalX=0 NormalY=0 NormalZ=1 AngleXU=0 Radius=1.65
    g6: Circle CenterX=-11.5625 CenterY=16.6378 CenterZ=0 NormalX=0 NormalY=0 NormalZ=1 AngleXU=0 Radius=1.65
    g7: Circle CenterX=-47.4641 CenterY=16.6426 CenterZ=0 NormalX=0 NormalY=0 NormalZ=1 AngleXU=0 Radius=1.65
  constraints (12):
    c: Diameter(g0) = 2.5
    c: Diameter(g1) = 2.5
    c: Diameter(g2) = 2.5
    c: Diameter(g3) = 2.5
    c: Diameter(g4) = 3.3
    c: Coincident(g4,g0)
    c: Diameter(g5) = 3.3
    c: Coincident(g5,g1)
    c: Diameter(g6) = 3.3
    c: Coincident(g6,g2)
    c: Diameter(g7) = 3.3
    c: Coincident(g7,g3)
FEATURE [Sketcher::SketchObject] Sketch012
  ArcFitTolerance = 1e-06
  AttachmentSupport = -> [Pocket001]
  FullyConstrained = false
  MakeInternals = false
  MapMode = 5
  Placement = pos=(0,2e-16,7.79) rot=(1,0,0;3.14159rad)
  sketch-geometry (4):
    g0: LineSegment StartX=-50.4523 StartY=48.4546 StartZ=0 EndX=-50.4523 EndY=13.6447 EndZ=0
    g1: LineSegment StartX=-50.4523 StartY=13.6447 StartZ=0 EndX=-8.56249 EndY=13.6447 EndZ=0
    g2: LineSegment StartX=-8.56249 StartY=13.6447 StartZ=0 EndX=-8.56249 EndY=48.4546 EndZ=0
    g3: LineSegment StartX=-8.56249 StartY=48.4546 StartZ=0 EndX=-50.4523 EndY=48.4546 EndZ=0
  constraints (8):
    c: Coincident(g0,g1)
    c: Coincident(g1,g2)
    c: Coincident(g2,g3)
    c: Coincident(g3,g0)
    c: Vertical(g0)
    c: Vertical(g2)
    c: Horizontal(g1)
    c: Horizontal(g3)
FEATURE [PartDesign::Pad] Pad002
  BaseFeature = -> Pocket001
  Direction = (0,0,-1)
  Length = 4
  Length2 = 10
  Profile = -> Sketch012
  ReferenceAxis = -> Sketch012 [N_Axis]
  Refine = true
  Reversed = true
  Suppressed = false
  Type = 0
FEATURE [PartDesign::Pocket] Pocket009
  BaseFeature = -> Pad002
  Direction = (0,0,1)
  Length = 3.3
  Length2 = 5
  Profile = -> Sketch011
  ReferenceAxis = -> Sketch011 [N_Axis]
  Refine = true
  Suppressed = false
  Type = 0
FEATURE [Sketcher::SketchObject] Sketch013
  ArcFitTolerance = 1e-06
  AttachmentSupport = -> [Pocket009]
  FullyConstrained = false
  MakeInternals = false
  MapMode = 5
  Placement = pos=(0,0,11.79) rot=(0,0,1;0rad)
  sketch-geometry (12):
    g0: LineSegment StartX=-40.4105 StartY=-24.0564 StartZ=0 EndX=-40.4105 EndY=-39.1305 EndZ=0
    g1: LineSegment StartX=-37.9275 StartY=-41.6135 StartZ=0 EndX=-20.5404 EndY=-41.6135 EndZ=0
    g2: LineSegment StartX=-18.0744 StartY=-39.1475 StartZ=0 EndX=-18.0744 EndY=-24.176 EndZ=0
    g3: LineSegment StartX=-20.9466 StartY=-21.3038 StartZ=0 EndX=-37.6578 EndY=-21.3038 EndZ=0
    g4: ArcOfCircle CenterX=-20.9466 CenterY=-24.176 CenterZ=0 NormalX=0 NormalY=0 NormalZ=1 AngleXU=0 Radius=2.87223 StartAngle=0 EndAngle=1.5708
    g5: GeomPoint [constr] X=-18.0744 Y=-21.3038 Z=0
    g6: ArcOfCircle CenterX=-37.6578 CenterY=-24.0564 CenterZ=0 NormalX=0 NormalY=0 NormalZ=1 AngleXU=0 Radius=2.75261 StartAngle=1.5708 EndAngle=3.14159
    g7: GeomPoint [constr] X=-40.4105 Y=-21.3038 Z=0
    g8: ArcOfCircle CenterX=-37.9275 CenterY=-39.1305 CenterZ=0 NormalX=0 NormalY=0 NormalZ=1 AngleXU=0 Radius=2.48295 StartAngle=3.14159 EndAngle=4.71239
    g9: GeomPoint [constr] X=-40.4105 Y=-41.6135 Z=0
    g10: ArcOfCircle CenterX=-20.5404 CenterY=-39.1475 CenterZ=0 NormalX=0 NormalY=0 NormalZ=1 AngleXU=0 Radius=2.46604 StartAngle=4.71239 EndAngle=6.28319
    g11: GeomPoint [constr] X=-18.0744 Y=-41.6135 Z=0
  constraints (20):
    c: Vertical(g0)
    c: Vertical(g2)
    c: Horizontal(g1)
    c: Horizontal(g3)
    c: PointOnObject(g5,g2)
    c: PointOnObject(g5,g3)
    c: Tangent(g2,g4) = -1.5708
    c: Tangent(g3,g4) = -1.5708
    c: PointOnObject(g7,g0)
    c: PointOnObject(g7,g3)
    c: Tangent(g0,g6) = -1.5708
    c: Tangent(g3,g6) = -1.5708
    c: PointOnObject(g9,g0)
    c: PointOnObject(g9,g1)
    c: Tangent(g0,g8) = -1.5708
    c: Tangent(g1,g8) = -1.5708
    c: PointOnObject(g11,g1)
    c: PointOnObject(g11,g2)
    c: Tangent(g1,g10) = -1.5708
    c: Tangent(g2,g10) = -1.5708
FEATURE [PartDesign::Pocket] Pocket010
  BaseFeature = -> Pocket009
  Direction = (0,0,-1)
  Length = 5
  Length2 = 5
  Profile = -> Sketch013
  ReferenceAxis = -> Sketch013 [N_Axis]
  Refine = true
  Suppressed = false
  Type = 1
FEATURE [PartDesign::Fillet] Fillet
  Base = -> Pocket010 [Edge155,Edge143,Edge152,Edge156]
  BaseFeature = -> Pocket010
  Radius = 3
  Refine = true
  SupportTransform = false
  Suppressed = false
  UseAllEdges = false
FEATURE [PartDesign::Body] Body
  AllowCompound = false
  BaseFeature = -> Part__Feature008
  Group = -> [BaseFeature,Sketch,Pad,Sketch001,Pocket,Sketch002,Pocket001,Sketch011,Sketch012,Pad002,Pocket009,Sketch013,Pocket010,Fillet]
  Origin = -> Origin004
  Placement = pos=(29,32,-7.8) rot=(0,0,1;0rad)
  Tip = -> Fillet
FEATURE [App::Part] Part  label="top-static"
  Group = -> [Part__Feature,Part__Feature001,Part__Feature003,Part__Feature004,Part__Feature006,Part__Feature007,Part__Feature009,Part__Feature008,Body]
  Origin = -> Origin
  Placement = pos=(0,-0.5,-0.2) rot=(0,0,1;0rad)
FEATURE [Part::Feature] Part__Feature030  label="Trackball001"
  shape: bbox 34 x 34 x 34 mm, 1 faces (baked)
FEATURE [Part::Feature] Part__Feature032  label="BTU housing"
  shape: bbox 8.956 x 9.626 x 9.54 mm, 6 faces (baked)
FEATURE [Part::Feature] Part__Feature034  label="BTU housing001"
  shape: bbox 8.956 x 9.626 x 9.54 mm, 6 faces (baked)
FEATURE [Part::Feature] Part__Feature035  label="BTU ball"
  shape: bbox 4 x 4 x 4 mm, 1 faces (baked)
FEATURE [Part::Feature] Part__Feature036  label="BTU housing002"
  shape: bbox 9 x 7.796 x 9.54 mm, 6 faces (baked)
FEATURE [Part::Feature] Part__Feature037  label="BTU ball001"
  shape: bbox 4 x 4 x 4 mm, 1 faces (baked)
FEATURE [Part::Feature] Part__Feature038  label="Trackball-holder001"
  shape: bbox 43.85 x 39.78 x 21.7 mm, 196 faces (baked)
FEATURE [Part::Feature] Part__Feature039  label="BTU ball002"
  shape: bbox 4 x 4 x 4 mm, 1 faces (baked)
FEATURE [Part::Feature] Part__Feature040  label="Trackball-holder002"
  shape: bbox 43.85 x 39.78 x 21.7 mm, 196 faces (baked)
FEATURE [PartDesign::FeatureBase] BaseFeature001
  BaseFeature = -> Part__Feature040
  Suppressed = false
FEATURE [Sketcher::SketchObject] Sketch014
  ArcFitTolerance = 1e-06
  AttachmentSupport = -> [BaseFeature001]
  ExternalGeometry = -> [BaseFeature001]
  FullyConstrained = true
  MakeInternals = false
  MapMode = 5
  Placement = pos=(0,0,13.79) rot=(1,0,0;3.14159rad)
  sketch-geometry (2):
    g0: Circle CenterX=-43.692 CenterY=31.5043 CenterZ=0 NormalX=0 NormalY=0 NormalZ=1 AngleXU=0 Radius=2.2
    g1: Circle CenterX=-14.692 CenterY=31.5043 CenterZ=0 NormalX=0 NormalY=0 NormalZ=1 AngleXU=0 Radius=2.2
  constraints (4):
    c: Coincident(g0,g-3)
    c: Equal(g0,g-3)
    c: Coincident(g1,g-4)
    c: Equal(g1,g-4)
FEATURE [PartDesign::Pad] Pad003
  BaseFeature = -> BaseFeature001
  Direction = (0,0,-1)
  Length = 6
  Length2 = 10
  Profile = -> Sketch014
  ReferenceAxis = -> Sketch014 [N_Axis]
  Refine = true
  Suppressed = false
  Type = 0
FEATURE [Sketcher::SketchObject] Sketch015
  ArcFitTolerance = 1e-06
  AttachmentSupport = -> [Pad003]
  FullyConstrained = false
  MakeInternals = false
  MapMode = 5
  Placement = pos=(0,0,11.29) rot=(1,0,0;3.14159rad)
  sketch-geometry (4):
    g0: LineSegment StartX=-41.9342 StartY=44.531 StartZ=0 EndX=-41.9342 EndY=19.2191 EndZ=0
    g1: LineSegment StartX=-41.9342 StartY=19.2191 StartZ=0 EndX=-17.3151 EndY=19.2191 EndZ=0
    g2: LineSegment StartX=-17.3151 StartY=19.2191 StartZ=0 EndX=-17.3151 EndY=44.531 EndZ=0
    g3: LineSegment StartX=-17.3151 StartY=44.531 StartZ=0 EndX=-41.9342 EndY=44.531 EndZ=0
  constraints (8):
    c: Coincident(g0,g1)
    c: Coincident(g1,g2)
    c: Coincident(g2,g3)
    c: Coincident(g3,g0)
    c: Vertical(g0)
    c: Vertical(g2)
    c: Horizontal(g1)
    c: Horizontal(g3)
FEATURE [Sketcher::SketchObject] Sketch016
  ArcFitTolerance = 1e-06
  AttachmentOffset = pos=(0,0,0.1) rot=(0,0,1;0rad)
  AttachmentSupport = -> [Pad003]
  FullyConstrained = false
  MakeInternals = false
  MapMode = 5
  Placement = pos=(0,2e-16,7.69) rot=(1,0,0;3.14159rad)
  sketch-geometry (12):
    g0: LineSegment StartX=-8.96251 StartY=17.9714 StartZ=0 EndX=-8.96251 EndY=43.6319 EndZ=0
    g1: LineSegment StartX=-13.8854 StartY=48.5548 StartZ=0 EndX=-45.9296 EndY=48.5548 EndZ=0
    g2: LineSegment StartX=-50.8525 StartY=43.6319 StartZ=0 EndX=-50.8525 EndY=17.9714 EndZ=0
    g3: LineSegment StartX=-46.6258 StartY=13.7448 StartZ=0 EndX=-13.1892 EndY=13.7448 EndZ=0
    g4: ArcOfCircle CenterX=-45.9296 CenterY=43.6319 CenterZ=0 NormalX=0 NormalY=0 NormalZ=1 AngleXU=0 Radius=4.92288 StartAngle=1.5708 EndAngle=3.14159
    g5: GeomPoint [constr] X=-50.8525 Y=48.5548 Z=0
    g6: ArcOfCircle CenterX=-13.8854 CenterY=43.6319 CenterZ=0 NormalX=0 NormalY=0 NormalZ=1 AngleXU=0 Radius=4.92288 StartAngle=0 EndAngle=1.5708
    g7: GeomPoint [constr] X=-8.96251 Y=48.5548 Z=0
    g8: ArcOfCircle CenterX=-13.1892 CenterY=17.9714 CenterZ=0 NormalX=0 NormalY=0 NormalZ=1 AngleXU=0 Radius=4.22668 StartAngle=4.71239 EndAngle=6.28319
    g9: GeomPoint [constr] X=-8.96251 Y=13.7448 Z=0
    g10: ArcOfCircle CenterX=-46.6258 CenterY=17.9714 CenterZ=0 NormalX=0 NormalY=0 NormalZ=1 AngleXU=0 Radius=4.22668 StartAngle=3.14159 EndAngle=4.71239
    g11: GeomPoint [constr] X=-50.8525 Y=13.7448 Z=0
  constraints (22):
    c: Vertical(g0)
    c: Vertical(g2)
    c: Horizontal(g1)
    c: Horizontal(g3)
    c: DistanceX(g5,g7) = 41.89
    c: DistanceY(g9,g7) = 34.81
    c: PointOnObject(g5,g1)
    c: PointOnObject(g5,g2)
    c: Tangent(g1,g4) = -1.5708
    c: Tangent(g2,g4) = -1.5708
    c: PointOnObject(g7,g0)
    c: PointOnObject(g7,g1)
    c: Tangent(g0,g6) = -1.5708
    c: Tangent(g1,g6) = -1.5708
    c: PointOnObject(g9,g0)
    c: PointOnObject(g9,g3)
    c: Tangent(g0,g8) = -1.5708
    c: Tangent(g3,g8) = -1.5708
    c: PointOnObject(g11,g2)
    c: PointOnObject(g11,g3)
    c: Tangent(g2,g10) = -1.5708
    c: Tangent(g3,g10) = -1.5708
FEATURE [PartDesign::Pad] Pad004
  BaseFeature = -> Pad003
  Direction = (0,0,-1)
  Length = 4
  Length2 = 10
  Profile = -> Sketch016
  ReferenceAxis = -> Sketch016 [N_Axis]
  Refine = true
  Reversed = true
  Suppressed = false
  Type = 0
FEATURE [PartDesign::SubShapeBinder] Binder
  BindCopyOnChange = 0
  BindMode = 0
  ClaimChildren = false
  Context = -> Part001 [Part002.Body003.Binder.]
  Fuse = false
  MakeFace = true
  OffsetFill = false
  OffsetIntersection = false
  OffsetJoinType = 0
  OffsetOpenResult = false
  PartialLoad = false
  Refine = true
  Relative = true
  Support = -> [Body001]
  _Version = 2
FEATURE [Sketcher::SketchObject] Sketch017
  ArcFitTolerance = 1e-06
  AttachmentSupport = -> [Pad004]
  ExternalGeometry = -> [Binder]
  FullyConstrained = true
  MakeInternals = false
  MapMode = 5
  Placement = pos=(0,0,7.69) rot=(1,0,0;3.14159rad)
  sketch-geometry (4):
    g0: Circle CenterX=-47.8525 CenterY=45.5547 CenterZ=0 NormalX=0 NormalY=0 NormalZ=1 AngleXU=0 Radius=1.65
    g1: Circle CenterX=-11.9625 CenterY=45.5547 CenterZ=0 NormalX=0 NormalY=0 NormalZ=1 AngleXU=0 Radius=1.65
    g2: Circle CenterX=-11.9625 CenterY=16.7447 CenterZ=0 NormalX=0 NormalY=0 NormalZ=1 AngleXU=0 Radius=1.65
    g3: Circle CenterX=-47.8525 CenterY=16.7447 CenterZ=0 NormalX=0 NormalY=0 NormalZ=1 AngleXU=0 Radius=1.65
  constraints (8):
    c: Diameter(g0) = 3.3
    c: Coincident(g0,g-3)
    c: Diameter(g1) = 3.3
    c: Coincident(g1,g-4)
    c: Diameter(g2) = 3.3
    c: Coincident(g2,g-5)
    c: Diameter(g3) = 3.3
    c: Coincident(g3,g-6)
FEATURE [PartDesign::Pocket] Pocket011
  BaseFeature = -> Pad004
  Direction = (0,0,1)
  Length = 3.3
  Length2 = 5
  Profile = -> Sketch017
  ReferenceAxis = -> Sketch017 [N_Axis]
  Refine = true
  Suppressed = false
  Type = 0
FEATURE [PartDesign::Pocket] Pocket012
  BaseFeature = -> Pocket011
  Direction = (0,0,1)
  Length = 5
  Length2 = 5
  Profile = -> Sketch015
  ReferenceAxis = -> Sketch015 [N_Axis]
  Refine = true
  Reversed = true
  Suppressed = false
  Type = 0
FEATURE [Sketcher::SketchObject] Sketch018
  ArcFitTolerance = 1e-06
  AttachmentSupport = -> [Pocket012]
  ExternalGeometry = -> [Pocket012]
  FullyConstrained = true
  MakeInternals = false
  MapMode = 5
  Placement = pos=(0,0,11.69) rot=(0,0,1;0rad)
  sketch-geometry (1):
    g0: Circle CenterX=-29.192 CenterY=-31.5043 CenterZ=0 NormalX=0 NormalY=0 NormalZ=1 AngleXU=0 Radius=6.25
  constraints (2):
    c: Coincident(g0,g-3)
    c: Equal(g0,g-3)
FEATURE [PartDesign::Pocket] Pocket013
  BaseFeature = -> Pocket012
  Direction = (0,0,-1)
  Length = 5
  Length2 = 5
  Profile = -> Sketch018
  ReferenceAxis = -> Sketch018 [N_Axis]
  Refine = true
  Suppressed = false
  Type = 0
FEATURE [PartDesign::Chamfer] Chamfer001
  Angle = 45
  Base = -> Pocket013 [Edge61]
  BaseFeature = -> Pocket013
  ChamferType = 0
  FlipDirection = false
  Refine = true
  Size = 1
  Size2 = 1
  SupportTransform = false
  Suppressed = false
  UseAllEdges = false
FEATURE [PartDesign::Body] Body003  label="btu top"
  AllowCompound = false
  BaseFeature = -> Part__Feature040
  Group = -> [BaseFeature001,Sketch014,Pad003,Sketch016,Pad004,Binder,Sketch017,Pocket011,Sketch015,Pocket012,Sketch018,Pocket013,Chamfer001]
  Origin = -> Origin008
  Tip = -> Chamfer001
FEATURE [App::Part] Part002  label="top-btu"
  Group = -> [Part__Feature030,Part__Feature032,Part__Feature034,Part__Feature035,Part__Feature036,Part__Feature037,Part__Feature039,Part__Feature038,Part__Feature040,Body003]
  Origin = -> Origin006
  Placement = pos=(29.4,31.6,-4) rot=(0,0,1;0rad)
FEATURE [App::Part] Part001  label="case"
  Group = -> [Body001,Part002,Part]
  Origin = -> Origin003
